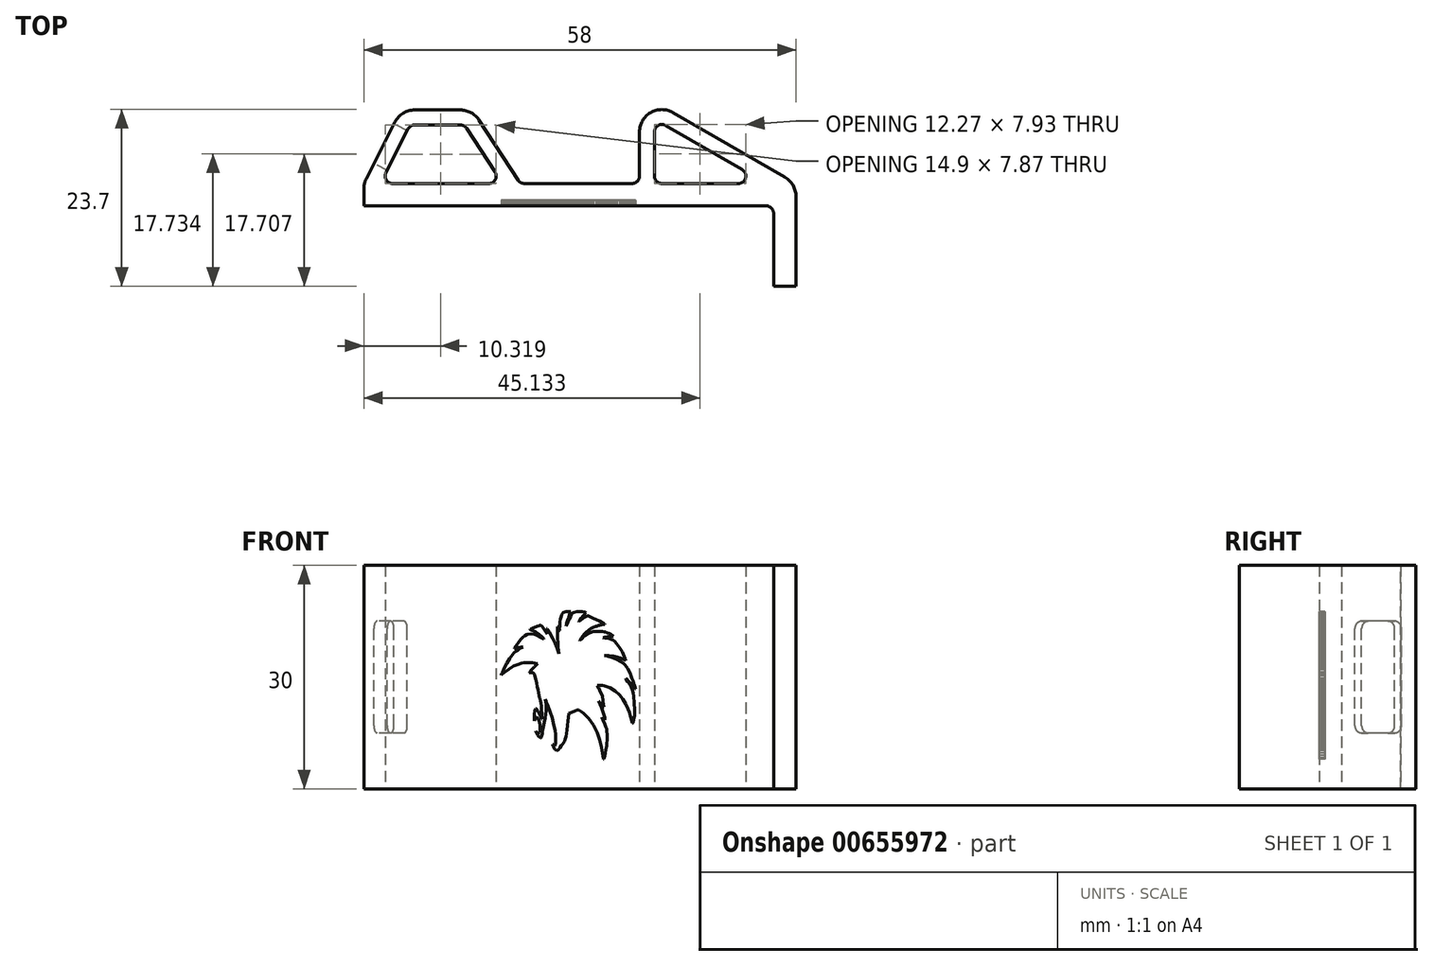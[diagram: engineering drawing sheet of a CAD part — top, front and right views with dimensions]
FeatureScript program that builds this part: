
annotation { "Feature Type Name" : "Feature", "Feature Type Description" : "" }
export const myFeature = defineFeature(function(context is Context, id is Id, definition is map)
    precondition{}
    {
        {
            assignVariable(context, id + "F0", {"name" : "SmallThickness", "anyValue" : 2 * mm});
        }
        {
            assignVariable(context, id + "F1", {"name" : "BatteryWidth", "anyValue" : 30});
        }
        {
            assignVariable(context, id + "F2", {"name" : "OuterFilet", "anyValue" : 3});
        }
        {
            assignVariable(context, id + "F3", {"name" : "InnerFilet", "anyValue" : 1 * mm});
        }
        {
            var Q0;
            Q0=qCreatedBy(makeId("Top.planeOp"),FACE);
            var sketch = newSketch(context, id + "F4", { "sketchPlane" : qUnion([Q0])});
            skLineSegment(sketch, "E0", {"start": v(-24, 9.87) * mm, "end": v(-29, 0) * mm});
            skLineSegment(sketch, "E1", {"start": v(-10.39, 0) * mm, "end": v(-15.5, 7.87) * mm});
            skLineSegment(sketch, "E2", {"start": v(-22.77, 7.87) * mm, "end": v(-26.76, 0) * mm});
            skLineSegment(sketch, "E3", {"start": v(-8, 0) * mm, "end": v(8, 0) * mm});
            skLineSegment(sketch, "E4", {"start": v(29, 0) * mm, "end": v(-29, 0) * mm, "construction": true});
            skLineSegment(sketch, "E5", {"start": v(10, 0) * mm, "end": v(25, 0) * mm});
            skLineSegment(sketch, "E6", {"start": v(29, 0) * mm, "end": v(8, 12.12) * mm});
            skLineSegment(sketch, "E7", {"start": v(8, 0) * mm, "end": v(8, 12.12) * mm});
            skLineSegment(sketch, "E8", {"start": v(10, 0) * mm, "end": v(10, 8.66) * mm});
            skLineSegment(sketch, "E9", {"start": v(10, 8.66) * mm, "end": v(25, 0) * mm});
            skLineSegment(sketch, "E10", {"start": v(42.35, 12.12) * mm, "end": v(-35.52, 12.12) * mm, "construction": true});
            skLineSegment(sketch, "E11", {"start": v(29, 0) * mm, "end": v(29, -13.77) * mm});
            skLineSegment(sketch, "E12", {"start": v(29, -13.77) * mm, "end": v(26, -13.77) * mm});
            skLineSegment(sketch, "E13", {"start": v(26, -13.77) * mm, "end": v(26, -3) * mm});
            skLineSegment(sketch, "E14", {"start": v(26, -3) * mm, "end": v(-29, -3) * mm});
            skLineSegment(sketch, "E15", {"start": v(-29, 0) * mm, "end": v(-29, -3) * mm});
            skLineSegment(sketch, "E16", {"start": v(-10.39, 0) * mm, "end": v(-26.76, 0) * mm});
            skLineSegment(sketch, "E17", {"start": v(25, 0) * mm, "end": v(10, 0) * mm});
            skLineSegment(sketch, "E18", {"start": v(-18.21, 9.87) * mm, "end": v(-18.21, 7.87) * mm, "construction": true});
            skLineSegment(sketch, "E19", {"start": v(-15.5, 7.87) * mm, "end": v(-22.77, 7.87) * mm});
            skLineSegment(sketch, "E20", {"start": v(-24, 9.87) * mm, "end": v(-14.42, 9.87) * mm});
            skLineSegment(sketch, "E21", {"start": v(-14.42, 9.87) * mm, "end": v(-8, 0) * mm});
            skSolve(sketch);
        }
        {
            var Q0;
            Q0 = qSketchRegion(id + "F4", true);
            extrude(context, id + "F5", {"entities" : qUnion([Q0]), "depth" : (getVariable(context, 'BatteryWidth')) * mm, "offsetDistance" : 25 * mm});
        }
        {
            var Q0;
            Q0=makeQuery(id+"F5.opExtrude","SWEPT_FACE",FACE,{"disambiguationData":[OSD([sQuery(id+"F4.wireOp",EDGE,"E14")])]});
            var sketch = newSketch(context, id + "F6", { "sketchPlane" : qUnion([Q0])});
            skLineSegment(sketch, "E22", {"start": v(-5.75, 22.15) * mm, "end": v(-5.57, 22.24) * mm});
            skLineSegment(sketch, "E23", {"start": v(-5.57, 22.24) * mm, "end": v(-5.41, 22.3) * mm});
            skLineSegment(sketch, "E24", {"start": v(-5.41, 22.3) * mm, "end": v(-5.32, 22.34) * mm});
            skLineSegment(sketch, "E25", {"start": v(-5.32, 22.34) * mm, "end": v(-5.3, 22.34) * mm});
            skLineSegment(sketch, "E26", {"start": v(-5.3, 22.34) * mm, "end": v(-5.3, 22.34) * mm});
            skLineSegment(sketch, "E27", {"start": v(-6.38, 21.9) * mm, "end": v(-6.07, 22) * mm});
            skLineSegment(sketch, "E28", {"start": v(-6.07, 22) * mm, "end": v(-5.75, 22.15) * mm});
            skLineSegment(sketch, "E29", {"start": v(-7.19, 21.57) * mm, "end": v(-7, 21.68) * mm});
            skLineSegment(sketch, "E30", {"start": v(-7, 21.68) * mm, "end": v(-6.74, 21.79) * mm});
            skLineSegment(sketch, "E31", {"start": v(-6.74, 21.79) * mm, "end": v(-6.55, 21.86) * mm});
            skLineSegment(sketch, "E32", {"start": v(-6.55, 21.86) * mm, "end": v(-6.38, 21.9) * mm});
            skLineSegment(sketch, "E33", {"start": v(-7.3, 21.42) * mm, "end": v(-7.26, 21.5) * mm});
            skLineSegment(sketch, "E34", {"start": v(-7.26, 21.5) * mm, "end": v(-7.19, 21.57) * mm});
            skLineSegment(sketch, "E35", {"start": v(-7.19, 21.37) * mm, "end": v(-7.28, 21.36) * mm});
            skLineSegment(sketch, "E36", {"start": v(-7.28, 21.36) * mm, "end": v(-7.3, 21.36) * mm});
            skLineSegment(sketch, "E37", {"start": v(-7.3, 21.36) * mm, "end": v(-7.32, 21.38) * mm});
            skLineSegment(sketch, "E38", {"start": v(-7.32, 21.38) * mm, "end": v(-7.3, 21.42) * mm});
            skLineSegment(sketch, "E39", {"start": v(-7.02, 21.3) * mm, "end": v(-7.07, 21.38) * mm});
            skLineSegment(sketch, "E40", {"start": v(-7.07, 21.38) * mm, "end": v(-7.19, 21.37) * mm});
            skLineSegment(sketch, "E41", {"start": v(-7.13, 21.14) * mm, "end": v(-7.06, 21.14) * mm});
            skLineSegment(sketch, "E42", {"start": v(-7.06, 21.14) * mm, "end": v(-7.03, 21.18) * mm});
            skLineSegment(sketch, "E43", {"start": v(-7.03, 21.18) * mm, "end": v(-7.02, 21.3) * mm});
            skLineSegment(sketch, "E44", {"start": v(-7.76, 20.68) * mm, "end": v(-7.5, 20.92) * mm});
            skLineSegment(sketch, "E45", {"start": v(-7.5, 20.92) * mm, "end": v(-7.32, 21.06) * mm});
            skLineSegment(sketch, "E46", {"start": v(-7.32, 21.06) * mm, "end": v(-7.21, 21.12) * mm});
            skLineSegment(sketch, "E47", {"start": v(-7.21, 21.12) * mm, "end": v(-7.13, 21.14) * mm});
            skLineSegment(sketch, "E48", {"start": v(-9.2, 18.81) * mm, "end": v(-8.9, 19.34) * mm});
            skLineSegment(sketch, "E49", {"start": v(-8.9, 19.34) * mm, "end": v(-8.5, 19.88) * mm});
            skLineSegment(sketch, "E50", {"start": v(-8.5, 19.88) * mm, "end": v(-7.76, 20.68) * mm});
            skLineSegment(sketch, "E51", {"start": v(-9.32, 18.57) * mm, "end": v(-9.2, 18.81) * mm});
            skLineSegment(sketch, "E52", {"start": v(-9.23, 18.5) * mm, "end": v(-9.32, 18.57) * mm});
            skLineSegment(sketch, "E53", {"start": v(-9.14, 18.43) * mm, "end": v(-9.23, 18.5) * mm});
            skLineSegment(sketch, "E54", {"start": v(-9.39, 18.09) * mm, "end": v(-9.14, 18.43) * mm});
            skLineSegment(sketch, "E55", {"start": v(-10.95, 14.96) * mm, "end": v(-10.65, 15.84) * mm});
            skLineSegment(sketch, "E56", {"start": v(-10.65, 15.84) * mm, "end": v(-10.23, 16.74) * mm});
            skLineSegment(sketch, "E57", {"start": v(-10.23, 16.74) * mm, "end": v(-9.83, 17.44) * mm});
            skLineSegment(sketch, "E58", {"start": v(-9.83, 17.44) * mm, "end": v(-9.39, 18.09) * mm});
            skLineSegment(sketch, "E59", {"start": v(3.79, 5.7) * mm, "end": v(3.7, 5.11) * mm});
            skLineSegment(sketch, "E60", {"start": v(3.7, 5.11) * mm, "end": v(3.56, 4.55) * mm});
            skLineSegment(sketch, "E61", {"start": v(3.56, 4.55) * mm, "end": v(3.42, 4.05) * mm});
            skLineSegment(sketch, "E62", {"start": v(3.42, 4.05) * mm, "end": v(3.32, 3.78) * mm});
            skLineSegment(sketch, "E63", {"start": v(3.32, 3.78) * mm, "end": v(3.23, 3.58) * mm});
            skLineSegment(sketch, "E64", {"start": v(3.23, 3.58) * mm, "end": v(3.15, 3.46) * mm});
            skLineSegment(sketch, "E65", {"start": v(3.15, 3.46) * mm, "end": v(3.1, 3.42) * mm});
            skLineSegment(sketch, "E66", {"start": v(3.8, 7.68) * mm, "end": v(3.83, 7.37) * mm});
            skLineSegment(sketch, "E67", {"start": v(3.83, 7.37) * mm, "end": v(3.84, 6.99) * mm});
            skLineSegment(sketch, "E68", {"start": v(3.84, 6.99) * mm, "end": v(3.84, 6.57) * mm});
            skLineSegment(sketch, "E69", {"start": v(3.84, 6.57) * mm, "end": v(3.82, 6.1) * mm});
            skLineSegment(sketch, "E70", {"start": v(3.82, 6.1) * mm, "end": v(3.79, 5.7) * mm});
            skArc(sketch, "E71", {"start": v(3.8, 7.68) * mm, "mid": v(3.76, 7.99) * mm, "end": v(3.7, 8.3) * mm});
            skArc(sketch, "E72", {"start": v(3.61, 9.04) * mm, "mid": v(3.64, 8.66) * mm, "end": v(3.7, 8.3) * mm});
            skArc(sketch, "E73", {"start": v(3.61, 9.04) * mm, "mid": v(3.59, 9.46) * mm, "end": v(3.5, 9.87) * mm});
            skLineSegment(sketch, "E74", {"start": v(3.44, 10.35) * mm, "end": v(3.43, 10.29) * mm});
            skLineSegment(sketch, "E75", {"start": v(3.43, 10.29) * mm, "end": v(3.44, 10.18) * mm});
            skLineSegment(sketch, "E76", {"start": v(3.44, 10.18) * mm, "end": v(3.46, 10.05) * mm});
            skLineSegment(sketch, "E77", {"start": v(3.46, 10.05) * mm, "end": v(3.5, 9.87) * mm});
            skLineSegment(sketch, "E78", {"start": v(3.07, 13.05) * mm, "end": v(3.22, 12.48) * mm});
            skLineSegment(sketch, "E79", {"start": v(3.22, 12.48) * mm, "end": v(3.35, 11.86) * mm});
            skLineSegment(sketch, "E80", {"start": v(3.35, 11.86) * mm, "end": v(3.43, 11.25) * mm});
            skLineSegment(sketch, "E81", {"start": v(3.43, 11.25) * mm, "end": v(3.47, 10.9) * mm});
            skLineSegment(sketch, "E82", {"start": v(3.47, 10.9) * mm, "end": v(3.48, 10.62) * mm});
            skLineSegment(sketch, "E83", {"start": v(3.48, 10.62) * mm, "end": v(3.47, 10.44) * mm});
            skLineSegment(sketch, "E84", {"start": v(3.47, 10.44) * mm, "end": v(3.44, 10.35) * mm});
            skArc(sketch, "E85", {"start": v(3.07, 13.05) * mm, "mid": v(3, 13.29) * mm, "end": v(2.92, 13.52) * mm});
            skLineSegment(sketch, "E86", {"start": v(3.09, 13.57) * mm, "end": v(2.96, 13.58) * mm});
            skLineSegment(sketch, "E87", {"start": v(2.96, 13.58) * mm, "end": v(2.92, 13.57) * mm});
            skLineSegment(sketch, "E88", {"start": v(2.92, 13.57) * mm, "end": v(2.91, 13.57) * mm});
            skLineSegment(sketch, "E89", {"start": v(2.91, 13.57) * mm, "end": v(2.91, 13.56) * mm});
            skLineSegment(sketch, "E90", {"start": v(2.91, 13.56) * mm, "end": v(2.92, 13.52) * mm});
            skLineSegment(sketch, "E91", {"start": v(5.54, 11.83) * mm, "end": v(4.9, 12.57) * mm});
            skLineSegment(sketch, "E92", {"start": v(4.9, 12.57) * mm, "end": v(4.2, 13.13) * mm});
            skLineSegment(sketch, "E93", {"start": v(4.2, 13.13) * mm, "end": v(3.63, 13.43) * mm});
            skLineSegment(sketch, "E94", {"start": v(3.63, 13.43) * mm, "end": v(3.09, 13.57) * mm});
            skLineSegment(sketch, "E95", {"start": v(7, 8.43) * mm, "end": v(6.68, 9.51) * mm});
            skLineSegment(sketch, "E96", {"start": v(6.68, 9.51) * mm, "end": v(6.29, 10.51) * mm});
            skLineSegment(sketch, "E97", {"start": v(6.29, 10.51) * mm, "end": v(5.93, 11.22) * mm});
            skLineSegment(sketch, "E98", {"start": v(5.93, 11.22) * mm, "end": v(5.54, 11.83) * mm});
            skLineSegment(sketch, "E99", {"start": v(7.14, 7.93) * mm, "end": v(7.14, 7.94) * mm});
            skLineSegment(sketch, "E100", {"start": v(7.14, 7.94) * mm, "end": v(7.14, 7.94) * mm});
            skLineSegment(sketch, "E101", {"start": v(7.14, 7.94) * mm, "end": v(7.12, 7.97) * mm});
            skLineSegment(sketch, "E102", {"start": v(7.12, 7.97) * mm, "end": v(7.1, 8.08) * mm});
            skLineSegment(sketch, "E103", {"start": v(7.1, 8.08) * mm, "end": v(7, 8.43) * mm});
            skLineSegment(sketch, "E104", {"start": v(7.44, 8.87) * mm, "end": v(7.28, 8.29) * mm});
            skLineSegment(sketch, "E105", {"start": v(7.28, 8.29) * mm, "end": v(7.2, 8.04) * mm});
            skLineSegment(sketch, "E106", {"start": v(7.2, 8.04) * mm, "end": v(7.16, 7.96) * mm});
            skLineSegment(sketch, "E107", {"start": v(7.16, 7.96) * mm, "end": v(7.15, 7.94) * mm});
            skLineSegment(sketch, "E108", {"start": v(7.15, 7.94) * mm, "end": v(7.14, 7.93) * mm});
            skLineSegment(sketch, "E109", {"start": v(7.57, 12.05) * mm, "end": v(7.6, 11.12) * mm});
            skLineSegment(sketch, "E110", {"start": v(7.6, 11.12) * mm, "end": v(7.59, 10.16) * mm});
            skLineSegment(sketch, "E111", {"start": v(7.59, 10.16) * mm, "end": v(7.53, 9.46) * mm});
            skLineSegment(sketch, "E112", {"start": v(7.53, 9.46) * mm, "end": v(7.44, 8.87) * mm});
            skLineSegment(sketch, "E113", {"start": v(7.52, 12.7) * mm, "end": v(7.57, 12.05) * mm});
            skLineSegment(sketch, "E114", {"start": v(7.63, 12.94) * mm, "end": v(7.53, 12.87) * mm});
            skLineSegment(sketch, "E115", {"start": v(7.53, 12.87) * mm, "end": v(7.52, 12.7) * mm});
            skArc(sketch, "E116", {"start": v(7.63, 12.94) * mm, "mid": v(7.71, 12.98) * mm, "end": v(7.79, 13.02) * mm});
            skLineSegment(sketch, "E117", {"start": v(7.4, 14.63) * mm, "end": v(7.57, 14.1) * mm});
            skLineSegment(sketch, "E118", {"start": v(7.57, 14.1) * mm, "end": v(7.7, 13.59) * mm});
            skLineSegment(sketch, "E119", {"start": v(7.7, 13.59) * mm, "end": v(7.75, 13.37) * mm});
            skLineSegment(sketch, "E120", {"start": v(7.75, 13.37) * mm, "end": v(7.78, 13.2) * mm});
            skLineSegment(sketch, "E121", {"start": v(7.78, 13.2) * mm, "end": v(7.8, 13.06) * mm});
            skLineSegment(sketch, "E122", {"start": v(7.8, 13.06) * mm, "end": v(7.8, 13.03) * mm});
            skLineSegment(sketch, "E123", {"start": v(7.8, 13.03) * mm, "end": v(7.79, 13.02) * mm});
            skArc(sketch, "E124", {"start": v(7.4, 14.63) * mm, "mid": v(7.08, 15.51) * mm, "end": v(6.68, 16.37) * mm});
            skLineSegment(sketch, "E125", {"start": v(6.5, 16.88) * mm, "end": v(6.48, 16.84) * mm});
            skLineSegment(sketch, "E126", {"start": v(6.48, 16.84) * mm, "end": v(6.48, 16.78) * mm});
            skLineSegment(sketch, "E127", {"start": v(6.48, 16.78) * mm, "end": v(6.5, 16.7) * mm});
            skLineSegment(sketch, "E128", {"start": v(6.5, 16.7) * mm, "end": v(6.57, 16.57) * mm});
            skLineSegment(sketch, "E129", {"start": v(6.57, 16.57) * mm, "end": v(6.68, 16.37) * mm});
            skLineSegment(sketch, "E130", {"start": v(6.5, 17.17) * mm, "end": v(6.55, 17) * mm});
            skLineSegment(sketch, "E131", {"start": v(6.55, 17) * mm, "end": v(6.55, 16.94) * mm});
            skLineSegment(sketch, "E132", {"start": v(6.55, 16.94) * mm, "end": v(6.5, 16.88) * mm});
            skLineSegment(sketch, "E133", {"start": v(4.95, 20.01) * mm, "end": v(5.5, 19.3) * mm});
            skLineSegment(sketch, "E134", {"start": v(5.5, 19.3) * mm, "end": v(5.98, 18.47) * mm});
            skLineSegment(sketch, "E135", {"start": v(5.98, 18.47) * mm, "end": v(6.3, 17.8) * mm});
            skLineSegment(sketch, "E136", {"start": v(6.3, 17.8) * mm, "end": v(6.5, 17.17) * mm});
            skLineSegment(sketch, "E137", {"start": v(4.77, 20.46) * mm, "end": v(4.73, 20.38) * mm});
            skLineSegment(sketch, "E138", {"start": v(4.73, 20.38) * mm, "end": v(4.74, 20.3) * mm});
            skLineSegment(sketch, "E139", {"start": v(4.74, 20.3) * mm, "end": v(4.8, 20.18) * mm});
            skLineSegment(sketch, "E140", {"start": v(4.8, 20.18) * mm, "end": v(4.95, 20.01) * mm});
            skLineSegment(sketch, "E141", {"start": v(4.74, 20.76) * mm, "end": v(4.82, 20.6) * mm});
            skLineSegment(sketch, "E142", {"start": v(4.82, 20.6) * mm, "end": v(4.77, 20.46) * mm});
            skLineSegment(sketch, "E143", {"start": v(-2.9, 22.72) * mm, "end": v(-2.88, 22.85) * mm});
            skLineSegment(sketch, "E144", {"start": v(-2.88, 22.85) * mm, "end": v(-2.83, 23.05) * mm});
            skLineSegment(sketch, "E145", {"start": v(-2.83, 23.05) * mm, "end": v(-2.73, 23.46) * mm});
            skLineSegment(sketch, "E146", {"start": v(-3.06, 22.54) * mm, "end": v(-3, 22.49) * mm});
            skLineSegment(sketch, "E147", {"start": v(-3, 22.49) * mm, "end": v(-2.97, 22.49) * mm});
            skLineSegment(sketch, "E148", {"start": v(-2.97, 22.49) * mm, "end": v(-2.95, 22.52) * mm});
            skLineSegment(sketch, "E149", {"start": v(-2.95, 22.52) * mm, "end": v(-2.93, 22.57) * mm});
            skLineSegment(sketch, "E150", {"start": v(-2.93, 22.57) * mm, "end": v(-2.9, 22.72) * mm});
            skLineSegment(sketch, "E151", {"start": v(-3.15, 22.58) * mm, "end": v(-3.14, 22.6) * mm});
            skLineSegment(sketch, "E152", {"start": v(-3.14, 22.6) * mm, "end": v(-3.12, 22.6) * mm});
            skLineSegment(sketch, "E153", {"start": v(-3.12, 22.6) * mm, "end": v(-3.1, 22.6) * mm});
            skLineSegment(sketch, "E154", {"start": v(-3.1, 22.6) * mm, "end": v(-3.06, 22.54) * mm});
            skLineSegment(sketch, "E155", {"start": v(-3.27, 21.07) * mm, "end": v(-3.24, 21.65) * mm});
            skLineSegment(sketch, "E156", {"start": v(-3.24, 21.65) * mm, "end": v(-3.2, 22.14) * mm});
            skLineSegment(sketch, "E157", {"start": v(-3.2, 22.14) * mm, "end": v(-3.18, 22.45) * mm});
            skLineSegment(sketch, "E158", {"start": v(-3.18, 22.45) * mm, "end": v(-3.15, 22.58) * mm});
            skLineSegment(sketch, "E159", {"start": v(-3.34, 20.3) * mm, "end": v(-3.33, 20.3) * mm});
            skLineSegment(sketch, "E160", {"start": v(-3.33, 20.3) * mm, "end": v(-3.32, 20.34) * mm});
            skLineSegment(sketch, "E161", {"start": v(-3.32, 20.34) * mm, "end": v(-3.3, 20.43) * mm});
            skLineSegment(sketch, "E162", {"start": v(-3.3, 20.43) * mm, "end": v(-3.29, 20.6) * mm});
            skLineSegment(sketch, "E163", {"start": v(-3.29, 20.6) * mm, "end": v(-3.28, 20.8) * mm});
            skLineSegment(sketch, "E164", {"start": v(-3.28, 20.8) * mm, "end": v(-3.27, 21.07) * mm});
            skLineSegment(sketch, "E165", {"start": v(-3.73, 20.9) * mm, "end": v(-3.57, 20.6) * mm});
            skLineSegment(sketch, "E166", {"start": v(-3.57, 20.6) * mm, "end": v(-3.45, 20.4) * mm});
            skLineSegment(sketch, "E167", {"start": v(-3.45, 20.4) * mm, "end": v(-3.38, 20.32) * mm});
            skLineSegment(sketch, "E168", {"start": v(-3.38, 20.32) * mm, "end": v(-3.34, 20.3) * mm});
            skLineSegment(sketch, "E169", {"start": v(-5.3, 22.34) * mm, "end": v(-5.28, 22.33) * mm});
            skLineSegment(sketch, "E170", {"start": v(-5.28, 22.33) * mm, "end": v(-5.27, 22.32) * mm});
            skLineSegment(sketch, "E171", {"start": v(-5.27, 22.32) * mm, "end": v(-5.25, 22.3) * mm});
            skLineSegment(sketch, "E172", {"start": v(-5.25, 22.3) * mm, "end": v(-5.19, 22.23) * mm});
            skLineSegment(sketch, "E173", {"start": v(-5.19, 22.23) * mm, "end": v(-5.04, 22.05) * mm});
            skLineSegment(sketch, "E174", {"start": v(-5.04, 22.05) * mm, "end": v(-4.85, 21.85) * mm});
            skLineSegment(sketch, "E175", {"start": v(-4.85, 21.85) * mm, "end": v(-4.72, 21.79) * mm});
            skLineSegment(sketch, "E176", {"start": v(-4.72, 21.79) * mm, "end": v(-4.65, 21.83) * mm});
            skLineSegment(sketch, "E177", {"start": v(-4.65, 21.83) * mm, "end": v(-4.6, 22) * mm});
            skLineSegment(sketch, "E178", {"start": v(-4.6, 22) * mm, "end": v(-4.57, 22.08) * mm});
            skLineSegment(sketch, "E179", {"start": v(-4.57, 22.08) * mm, "end": v(-4.55, 22.1) * mm});
            skLineSegment(sketch, "E180", {"start": v(-4.55, 22.1) * mm, "end": v(-4.53, 22.11) * mm});
            skLineSegment(sketch, "E181", {"start": v(-4.53, 22.11) * mm, "end": v(-4.49, 22.1) * mm});
            skLineSegment(sketch, "E182", {"start": v(-4.49, 22.1) * mm, "end": v(-4.45, 22.06) * mm});
            skLineSegment(sketch, "E183", {"start": v(-4.45, 22.06) * mm, "end": v(-4.36, 21.95) * mm});
            skLineSegment(sketch, "E184", {"start": v(-4.36, 21.95) * mm, "end": v(-4.15, 21.65) * mm});
            skLineSegment(sketch, "E185", {"start": v(-4.15, 21.65) * mm, "end": v(-3.94, 21.3) * mm});
            skLineSegment(sketch, "E186", {"start": v(-3.94, 21.3) * mm, "end": v(-3.73, 20.9) * mm});
            skLineSegment(sketch, "E187", {"start": v(-2.73, 23.46) * mm, "end": v(-2.66, 23.72) * mm});
            skLineSegment(sketch, "E188", {"start": v(-2.66, 23.72) * mm, "end": v(-2.6, 23.9) * mm});
            skLineSegment(sketch, "E189", {"start": v(-2.6, 23.9) * mm, "end": v(-2.5, 24.06) * mm});
            skLineSegment(sketch, "E190", {"start": v(-2.5, 24.06) * mm, "end": v(-2.35, 24.12) * mm});
            skLineSegment(sketch, "E191", {"start": v(-2.35, 24.12) * mm, "end": v(-2.1, 24.17) * mm});
            skLineSegment(sketch, "E192", {"start": v(-2.1, 24.17) * mm, "end": v(-1.67, 24.23) * mm});
            skLineSegment(sketch, "E193", {"start": v(-1.67, 24.23) * mm, "end": v(-1.35, 24.25) * mm});
            skLineSegment(sketch, "E194", {"start": v(-1.35, 24.25) * mm, "end": v(-1.16, 24.25) * mm});
            skLineSegment(sketch, "E195", {"start": v(-1.16, 24.25) * mm, "end": v(-1.08, 24.22) * mm});
            skLineSegment(sketch, "E196", {"start": v(-1.08, 24.22) * mm, "end": v(-0.97, 24.18) * mm});
            skLineSegment(sketch, "E197", {"start": v(-0.97, 24.18) * mm, "end": v(-0.8, 24.18) * mm});
            skLineSegment(sketch, "E198", {"start": v(-0.8, 24.18) * mm, "end": v(-0.6, 24.2) * mm});
            skLineSegment(sketch, "E199", {"start": v(-0.6, 24.2) * mm, "end": v(-0.37, 24.23) * mm});
            skLineSegment(sketch, "E200", {"start": v(-0.37, 24.23) * mm, "end": v(0, 24.27) * mm});
            skLineSegment(sketch, "E201", {"start": v(0, 24.27) * mm, "end": v(0.4, 24.29) * mm});
            skLineSegment(sketch, "E202", {"start": v(0.4, 24.29) * mm, "end": v(0.67, 24.27) * mm});
            skLineSegment(sketch, "E203", {"start": v(0.67, 24.27) * mm, "end": v(0.86, 24.24) * mm});
            skLineSegment(sketch, "E204", {"start": v(0.86, 24.24) * mm, "end": v(1, 24.16) * mm});
            skLineSegment(sketch, "E205", {"start": v(1, 24.16) * mm, "end": v(1.04, 24.05) * mm});
            skLineSegment(sketch, "E206", {"start": v(1.04, 24.05) * mm, "end": v(1.12, 23.89) * mm});
            skLineSegment(sketch, "E207", {"start": v(1.12, 23.89) * mm, "end": v(1.25, 23.74) * mm});
            skLineSegment(sketch, "E208", {"start": v(1.25, 23.74) * mm, "end": v(1.56, 23.53) * mm});
            skLineSegment(sketch, "E209", {"start": v(1.56, 23.53) * mm, "end": v(2.2, 23.23) * mm});
            skLineSegment(sketch, "E210", {"start": v(2.2, 23.23) * mm, "end": v(2.72, 22.96) * mm});
            skLineSegment(sketch, "E211", {"start": v(2.72, 22.96) * mm, "end": v(3.16, 22.7) * mm});
            skLineSegment(sketch, "E212", {"start": v(3.16, 22.7) * mm, "end": v(3.58, 22.43) * mm});
            skLineSegment(sketch, "E213", {"start": v(3.58, 22.43) * mm, "end": v(3.92, 22.16) * mm});
            skLineSegment(sketch, "E214", {"start": v(3.92, 22.16) * mm, "end": v(4.11, 21.99) * mm});
            skLineSegment(sketch, "E215", {"start": v(4.11, 21.99) * mm, "end": v(4.02, 21.91) * mm});
            skLineSegment(sketch, "E216", {"start": v(4.02, 21.91) * mm, "end": v(3.88, 21.83) * mm});
            skLineSegment(sketch, "E217", {"start": v(3.88, 21.83) * mm, "end": v(3.7, 21.76) * mm});
            skLineSegment(sketch, "E218", {"start": v(3.7, 21.76) * mm, "end": v(3.27, 21.64) * mm});
            skLineSegment(sketch, "E219", {"start": v(3.27, 21.64) * mm, "end": v(3.17, 21.6) * mm});
            skLineSegment(sketch, "E220", {"start": v(3.17, 21.6) * mm, "end": v(3.16, 21.6) * mm});
            skLineSegment(sketch, "E221", {"start": v(3.16, 21.6) * mm, "end": v(3.15, 21.58) * mm});
            skLineSegment(sketch, "E222", {"start": v(3.15, 21.58) * mm, "end": v(3.17, 21.56) * mm});
            skLineSegment(sketch, "E223", {"start": v(3.17, 21.56) * mm, "end": v(3.21, 21.54) * mm});
            skLineSegment(sketch, "E224", {"start": v(3.21, 21.54) * mm, "end": v(3.4, 21.48) * mm});
            skLineSegment(sketch, "E225", {"start": v(3.4, 21.48) * mm, "end": v(3.8, 21.32) * mm});
            skLineSegment(sketch, "E226", {"start": v(3.8, 21.32) * mm, "end": v(4.22, 21.1) * mm});
            skLineSegment(sketch, "E227", {"start": v(4.22, 21.1) * mm, "end": v(4.52, 20.93) * mm});
            skLineSegment(sketch, "E228", {"start": v(4.52, 20.93) * mm, "end": v(4.74, 20.76) * mm});
            skLineSegment(sketch, "E229", {"start": v(3.1, 3.42) * mm, "end": v(3.09, 3.42) * mm});
            skLineSegment(sketch, "E230", {"start": v(3.09, 3.42) * mm, "end": v(3.08, 3.43) * mm});
            skLineSegment(sketch, "E231", {"start": v(3.08, 3.43) * mm, "end": v(3.05, 3.5) * mm});
            skLineSegment(sketch, "E232", {"start": v(3.05, 3.5) * mm, "end": v(3.03, 3.62) * mm});
            skLineSegment(sketch, "E233", {"start": v(3.03, 3.62) * mm, "end": v(2.78, 5.08) * mm});
            skLineSegment(sketch, "E234", {"start": v(2.78, 5.08) * mm, "end": v(2.42, 6.46) * mm});
            skLineSegment(sketch, "E235", {"start": v(2.42, 6.46) * mm, "end": v(2.08, 7.4) * mm});
            skLineSegment(sketch, "E236", {"start": v(2.08, 7.4) * mm, "end": v(1.7, 8.18) * mm});
            skLineSegment(sketch, "E237", {"start": v(1.7, 8.18) * mm, "end": v(1.37, 8.67) * mm});
            skLineSegment(sketch, "E238", {"start": v(1.37, 8.67) * mm, "end": v(0.99, 9.16) * mm});
            skLineSegment(sketch, "E239", {"start": v(0.99, 9.16) * mm, "end": v(0.6, 9.6) * mm});
            skLineSegment(sketch, "E240", {"start": v(0.6, 9.6) * mm, "end": v(0.35, 9.84) * mm});
            skLineSegment(sketch, "E241", {"start": v(0.35, 9.84) * mm, "end": v(0.14, 10.02) * mm});
            skLineSegment(sketch, "E242", {"start": v(0.14, 10.02) * mm, "end": v(0, 10.11) * mm});
            skLineSegment(sketch, "E243", {"start": v(0, 10.11) * mm, "end": v(-0.12, 10.16) * mm});
            skLineSegment(sketch, "E244", {"start": v(-0.12, 10.16) * mm, "end": v(-0.4, 10.15) * mm});
            skLineSegment(sketch, "E245", {"start": v(-0.4, 10.15) * mm, "end": v(-0.7, 10.05) * mm});
            skLineSegment(sketch, "E246", {"start": v(-0.7, 10.05) * mm, "end": v(-0.93, 9.91) * mm});
            skLineSegment(sketch, "E247", {"start": v(-0.93, 9.91) * mm, "end": v(-1.12, 9.75) * mm});
            skLineSegment(sketch, "E248", {"start": v(-1.12, 9.75) * mm, "end": v(-1.24, 9.56) * mm});
            skLineSegment(sketch, "E249", {"start": v(-1.24, 9.56) * mm, "end": v(-1.29, 9.34) * mm});
            skLineSegment(sketch, "E250", {"start": v(-1.29, 9.34) * mm, "end": v(-1.57, 7.23) * mm});
            skLineSegment(sketch, "E251", {"start": v(-1.57, 7.23) * mm, "end": v(-1.62, 6.8) * mm});
            skLineSegment(sketch, "E252", {"start": v(-1.62, 6.8) * mm, "end": v(-1.67, 6.5) * mm});
            skLineSegment(sketch, "E253", {"start": v(-1.67, 6.5) * mm, "end": v(-1.73, 6.28) * mm});
            skLineSegment(sketch, "E254", {"start": v(-1.73, 6.28) * mm, "end": v(-1.84, 6.08) * mm});
            skLineSegment(sketch, "E255", {"start": v(-1.84, 6.08) * mm, "end": v(-2, 5.87) * mm});
            skLineSegment(sketch, "E256", {"start": v(-2, 5.87) * mm, "end": v(-2.57, 5.17) * mm});
            skLineSegment(sketch, "E257", {"start": v(-2.57, 5.17) * mm, "end": v(-2.73, 4.96) * mm});
            skLineSegment(sketch, "E258", {"start": v(-2.73, 4.96) * mm, "end": v(-2.86, 4.82) * mm});
            skLineSegment(sketch, "E259", {"start": v(-2.86, 4.82) * mm, "end": v(-3, 4.7) * mm});
            skLineSegment(sketch, "E260", {"start": v(-3, 4.7) * mm, "end": v(-3.15, 4.69) * mm});
            skLineSegment(sketch, "E261", {"start": v(-3.15, 4.69) * mm, "end": v(-3.32, 4.8) * mm});
            skLineSegment(sketch, "E262", {"start": v(-3.32, 4.8) * mm, "end": v(-3.49, 4.97) * mm});
            skLineSegment(sketch, "E263", {"start": v(-3.49, 4.97) * mm, "end": v(-3.64, 5.24) * mm});
            skLineSegment(sketch, "E264", {"start": v(-3.64, 5.24) * mm, "end": v(-3.75, 5.52) * mm});
            skLineSegment(sketch, "E265", {"start": v(-3.75, 5.52) * mm, "end": v(-3.85, 5.85) * mm});
            skLineSegment(sketch, "E266", {"start": v(-3.85, 5.85) * mm, "end": v(-3.92, 6.11) * mm});
            skLineSegment(sketch, "E267", {"start": v(-3.92, 6.11) * mm, "end": v(-3.96, 6.3) * mm});
            skLineSegment(sketch, "E268", {"start": v(-3.96, 6.3) * mm, "end": v(-3.96, 6.41) * mm});
            skLineSegment(sketch, "E269", {"start": v(-3.96, 6.41) * mm, "end": v(-3.95, 6.46) * mm});
            skLineSegment(sketch, "E270", {"start": v(-3.95, 6.46) * mm, "end": v(-3.92, 6.48) * mm});
            skLineSegment(sketch, "E271", {"start": v(-3.92, 6.48) * mm, "end": v(-3.88, 6.48) * mm});
            skLineSegment(sketch, "E272", {"start": v(-3.88, 6.48) * mm, "end": v(-3.7, 6.4) * mm});
            skLineSegment(sketch, "E273", {"start": v(-3.7, 6.4) * mm, "end": v(-3.54, 6.3) * mm});
            skLineSegment(sketch, "E274", {"start": v(-3.54, 6.3) * mm, "end": v(-3.52, 6.44) * mm});
            skLineSegment(sketch, "E275", {"start": v(-3.52, 6.44) * mm, "end": v(-3.48, 6.73) * mm});
            skLineSegment(sketch, "E276", {"start": v(-3.48, 6.73) * mm, "end": v(-3.47, 6.97) * mm});
            skLineSegment(sketch, "E277", {"start": v(-3.47, 6.97) * mm, "end": v(-3.48, 7.17) * mm});
            skLineSegment(sketch, "E278", {"start": v(-3.48, 7.17) * mm, "end": v(-3.5, 7.4) * mm});
            skArc(sketch, "E279", {"start": v(-3.5, 7.4) * mm, "mid": v(-3.6, 8.14) * mm, "end": v(-3.77, 8.86) * mm});
            skLineSegment(sketch, "E280", {"start": v(-3.77, 8.86) * mm, "end": v(-4.05, 9.7) * mm});
            skLineSegment(sketch, "E281", {"start": v(-4.05, 9.7) * mm, "end": v(-4.19, 10.06) * mm});
            skLineSegment(sketch, "E282", {"start": v(-4.19, 10.06) * mm, "end": v(-4.23, 10.17) * mm});
            skLineSegment(sketch, "E283", {"start": v(-4.23, 10.17) * mm, "end": v(-4.25, 10.2) * mm});
            skLineSegment(sketch, "E284", {"start": v(-4.25, 10.2) * mm, "end": v(-4.26, 10.21) * mm});
            skLineSegment(sketch, "E285", {"start": v(-4.26, 10.21) * mm, "end": v(-4.27, 10.2) * mm});
            skLineSegment(sketch, "E286", {"start": v(-4.27, 10.2) * mm, "end": v(-4.29, 10.2) * mm});
            skLineSegment(sketch, "E287", {"start": v(-4.29, 10.2) * mm, "end": v(-4.34, 10.02) * mm});
            skLineSegment(sketch, "E288", {"start": v(-4.34, 10.02) * mm, "end": v(-4.44, 9.52) * mm});
            skLineSegment(sketch, "E289", {"start": v(-4.44, 9.52) * mm, "end": v(-4.73, 7.15) * mm});
            skLineSegment(sketch, "E290", {"start": v(-4.73, 7.15) * mm, "end": v(-4.78, 6.3) * mm});
            skLineSegment(sketch, "E291", {"start": v(-4.78, 6.3) * mm, "end": v(-4.83, 6.1) * mm});
            skLineSegment(sketch, "E292", {"start": v(-4.83, 6.1) * mm, "end": v(-4.9, 5.9) * mm});
            skLineSegment(sketch, "E293", {"start": v(-4.9, 5.9) * mm, "end": v(-4.96, 5.75) * mm});
            skLineSegment(sketch, "E294", {"start": v(-4.96, 5.75) * mm, "end": v(-5.01, 5.65) * mm});
            skLineSegment(sketch, "E295", {"start": v(-5.01, 5.65) * mm, "end": v(-5.08, 5.56) * mm});
            skLineSegment(sketch, "E296", {"start": v(-5.08, 5.56) * mm, "end": v(-5.2, 5.67) * mm});
            skArc(sketch, "E297", {"start": v(-5.48, 6.03) * mm, "mid": v(-5.35, 5.85) * mm, "end": v(-5.2, 5.67) * mm});
            skLineSegment(sketch, "E298", {"start": v(-5.48, 6.03) * mm, "end": v(-5.7, 6.37) * mm});
            skLineSegment(sketch, "E299", {"start": v(-5.7, 6.37) * mm, "end": v(-5.84, 6.67) * mm});
            skLineSegment(sketch, "E300", {"start": v(-5.84, 6.67) * mm, "end": v(-5.95, 7.14) * mm});
            skLineSegment(sketch, "E301", {"start": v(-5.95, 7.14) * mm, "end": v(-6.04, 7.46) * mm});
            skLineSegment(sketch, "E302", {"start": v(-6.04, 7.46) * mm, "end": v(-6.17, 7.78) * mm});
            skLineSegment(sketch, "E303", {"start": v(-6.17, 7.78) * mm, "end": v(-6.3, 8.08) * mm});
            skLineSegment(sketch, "E304", {"start": v(-6.3, 8.08) * mm, "end": v(-6.33, 8.18) * mm});
            skLineSegment(sketch, "E305", {"start": v(-6.33, 8.18) * mm, "end": v(-6.34, 8.2) * mm});
            skLineSegment(sketch, "E306", {"start": v(-6.34, 8.2) * mm, "end": v(-6.34, 8.21) * mm});
            skLineSegment(sketch, "E307", {"start": v(-6.34, 8.21) * mm, "end": v(-6.33, 8.21) * mm});
            skLineSegment(sketch, "E308", {"start": v(-6.33, 8.21) * mm, "end": v(-6.3, 8.2) * mm});
            skLineSegment(sketch, "E309", {"start": v(-6.3, 8.2) * mm, "end": v(-6.23, 8.18) * mm});
            skLineSegment(sketch, "E310", {"start": v(-6.23, 8.18) * mm, "end": v(-6, 8.08) * mm});
            skLineSegment(sketch, "E311", {"start": v(-6, 8.08) * mm, "end": v(-5.73, 7.96) * mm});
            skLineSegment(sketch, "E312", {"start": v(-5.73, 7.96) * mm, "end": v(-5.66, 7.95) * mm});
            skLineSegment(sketch, "E313", {"start": v(-5.66, 7.95) * mm, "end": v(-5.63, 7.96) * mm});
            skLineSegment(sketch, "E314", {"start": v(-5.63, 7.96) * mm, "end": v(-5.62, 7.97) * mm});
            skLineSegment(sketch, "E315", {"start": v(-5.62, 7.97) * mm, "end": v(-5.62, 8) * mm});
            skLineSegment(sketch, "E316", {"start": v(-5.62, 8) * mm, "end": v(-5.61, 8.04) * mm});
            skLineSegment(sketch, "E317", {"start": v(-5.61, 8.04) * mm, "end": v(-5.62, 8.18) * mm});
            skLineSegment(sketch, "E318", {"start": v(-5.62, 8.18) * mm, "end": v(-5.65, 8.5) * mm});
            skLineSegment(sketch, "E319", {"start": v(-5.65, 8.5) * mm, "end": v(-5.71, 8.84) * mm});
            skLineSegment(sketch, "E320", {"start": v(-5.71, 8.84) * mm, "end": v(-5.74, 8.96) * mm});
            skLineSegment(sketch, "E321", {"start": v(-5.74, 8.96) * mm, "end": v(-5.75, 9) * mm});
            skLineSegment(sketch, "E322", {"start": v(-5.75, 9) * mm, "end": v(-5.76, 9) * mm});
            skLineSegment(sketch, "E323", {"start": v(-5.76, 9) * mm, "end": v(-5.76, 9) * mm});
            skLineSegment(sketch, "E324", {"start": v(-5.76, 9) * mm, "end": v(-5.78, 9) * mm});
            skLineSegment(sketch, "E325", {"start": v(-5.78, 9) * mm, "end": v(-5.8, 8.99) * mm});
            skLineSegment(sketch, "E326", {"start": v(-5.8, 8.99) * mm, "end": v(-5.85, 8.93) * mm});
            skLineSegment(sketch, "E327", {"start": v(-5.85, 8.93) * mm, "end": v(-5.98, 8.73) * mm});
            skLineSegment(sketch, "E328", {"start": v(-5.98, 8.73) * mm, "end": v(-6.1, 8.55) * mm});
            skLineSegment(sketch, "E329", {"start": v(-6.1, 8.55) * mm, "end": v(-6.16, 8.49) * mm});
            skLineSegment(sketch, "E330", {"start": v(-6.16, 8.49) * mm, "end": v(-6.18, 8.48) * mm});
            skLineSegment(sketch, "E331", {"start": v(-6.18, 8.48) * mm, "end": v(-6.18, 8.48) * mm});
            skLineSegment(sketch, "E332", {"start": v(-6.18, 8.48) * mm, "end": v(-6.18, 8.49) * mm});
            skLineSegment(sketch, "E333", {"start": v(-6.18, 8.49) * mm, "end": v(-6.23, 8.7) * mm});
            skLineSegment(sketch, "E334", {"start": v(-6.23, 8.7) * mm, "end": v(-6.27, 9.04) * mm});
            skLineSegment(sketch, "E335", {"start": v(-6.27, 9.04) * mm, "end": v(-6.28, 9.37) * mm});
            skLineSegment(sketch, "E336", {"start": v(-6.28, 9.37) * mm, "end": v(-6.28, 9.74) * mm});
            skLineSegment(sketch, "E337", {"start": v(-6.28, 9.74) * mm, "end": v(-6.26, 10.15) * mm});
            skLineSegment(sketch, "E338", {"start": v(-6.26, 10.15) * mm, "end": v(-6.24, 10.44) * mm});
            skLineSegment(sketch, "E339", {"start": v(-6.24, 10.44) * mm, "end": v(-6.2, 10.66) * mm});
            skLineSegment(sketch, "E340", {"start": v(-6.2, 10.66) * mm, "end": v(-6.14, 10.92) * mm});
            skLineSegment(sketch, "E341", {"start": v(-6.14, 10.92) * mm, "end": v(-6.09, 11.14) * mm});
            skLineSegment(sketch, "E342", {"start": v(-6.09, 11.14) * mm, "end": v(-6.04, 11.32) * mm});
            skLineSegment(sketch, "E343", {"start": v(-6.04, 11.32) * mm, "end": v(-6, 11.42) * mm});
            skLineSegment(sketch, "E344", {"start": v(-6, 11.42) * mm, "end": v(-6, 11.44) * mm});
            skLineSegment(sketch, "E345", {"start": v(-6, 11.44) * mm, "end": v(-6, 11.45) * mm});
            skLineSegment(sketch, "E346", {"start": v(-6, 11.45) * mm, "end": v(-5.99, 11.46) * mm});
            skLineSegment(sketch, "E347", {"start": v(-5.99, 11.46) * mm, "end": v(-5.98, 11.45) * mm});
            skLineSegment(sketch, "E348", {"start": v(-5.98, 11.45) * mm, "end": v(-5.97, 11.44) * mm});
            skLineSegment(sketch, "E349", {"start": v(-5.97, 11.44) * mm, "end": v(-5.88, 11.36) * mm});
            skLineSegment(sketch, "E350", {"start": v(-5.88, 11.36) * mm, "end": v(-5.76, 11.2) * mm});
            skLineSegment(sketch, "E351", {"start": v(-5.76, 11.2) * mm, "end": v(-5.6, 11) * mm});
            skLineSegment(sketch, "E352", {"start": v(-5.6, 11) * mm, "end": v(-5.52, 10.94) * mm});
            skLineSegment(sketch, "E353", {"start": v(-5.52, 10.94) * mm, "end": v(-5.5, 10.94) * mm});
            skLineSegment(sketch, "E354", {"start": v(-5.5, 10.94) * mm, "end": v(-5.5, 10.95) * mm});
            skLineSegment(sketch, "E355", {"start": v(-5.5, 10.95) * mm, "end": v(-5.5, 10.99) * mm});
            skLineSegment(sketch, "E356", {"start": v(-5.5, 10.99) * mm, "end": v(-5.5, 11.03) * mm});
            skArc(sketch, "E357", {"start": v(-5.56, 11.42) * mm, "mid": v(-5.53, 11.23) * mm, "end": v(-5.5, 11.03) * mm});
            skLineSegment(sketch, "E358", {"start": v(-5.56, 11.42) * mm, "end": v(-5.62, 11.8) * mm});
            skLineSegment(sketch, "E359", {"start": v(-5.62, 11.8) * mm, "end": v(-5.7, 12.33) * mm});
            skLineSegment(sketch, "E360", {"start": v(-5.7, 12.33) * mm, "end": v(-5.82, 12.93) * mm});
            skLineSegment(sketch, "E361", {"start": v(-5.82, 12.93) * mm, "end": v(-5.93, 13.54) * mm});
            skLineSegment(sketch, "E362", {"start": v(-5.93, 13.54) * mm, "end": v(-6.03, 14.04) * mm});
            skLineSegment(sketch, "E363", {"start": v(-6.03, 14.04) * mm, "end": v(-6.11, 14.45) * mm});
            skLineSegment(sketch, "E364", {"start": v(-6.11, 14.45) * mm, "end": v(-6.16, 14.68) * mm});
            skLineSegment(sketch, "E365", {"start": v(-6.16, 14.68) * mm, "end": v(-6.2, 14.81) * mm});
            skArc(sketch, "E366", {"start": v(-6.2, 14.81) * mm, "mid": v(-6.27, 14.97) * mm, "end": v(-6.38, 15.1) * mm});
            skLineSegment(sketch, "E367", {"start": v(-6.38, 15.1) * mm, "end": v(-6.47, 15.17) * mm});
            skLineSegment(sketch, "E368", {"start": v(-6.47, 15.17) * mm, "end": v(-6.55, 15.2) * mm});
            skLineSegment(sketch, "E369", {"start": v(-6.55, 15.2) * mm, "end": v(-6.62, 15.2) * mm});
            skLineSegment(sketch, "E370", {"start": v(-6.62, 15.2) * mm, "end": v(-6.74, 15.2) * mm});
            skLineSegment(sketch, "E371", {"start": v(-6.74, 15.2) * mm, "end": v(-6.97, 15.18) * mm});
            skLineSegment(sketch, "E372", {"start": v(-6.97, 15.18) * mm, "end": v(-7, 15.28) * mm});
            skLineSegment(sketch, "E373", {"start": v(-7, 15.28) * mm, "end": v(-7, 15.54) * mm});
            skLineSegment(sketch, "E374", {"start": v(-7, 15.54) * mm, "end": v(-6.9, 15.87) * mm});
            skLineSegment(sketch, "E375", {"start": v(-6.9, 15.87) * mm, "end": v(-6.65, 16.4) * mm});
            skLineSegment(sketch, "E376", {"start": v(-6.65, 16.4) * mm, "end": v(-6.57, 16.52) * mm});
            skLineSegment(sketch, "E377", {"start": v(-6.57, 16.52) * mm, "end": v(-6.54, 16.58) * mm});
            skLineSegment(sketch, "E378", {"start": v(-6.54, 16.58) * mm, "end": v(-6.54, 16.61) * mm});
            skLineSegment(sketch, "E379", {"start": v(-6.54, 16.61) * mm, "end": v(-6.56, 16.63) * mm});
            skLineSegment(sketch, "E380", {"start": v(-6.56, 16.63) * mm, "end": v(-6.66, 16.64) * mm});
            skLineSegment(sketch, "E381", {"start": v(-6.66, 16.64) * mm, "end": v(-6.8, 16.65) * mm});
            skLineSegment(sketch, "E382", {"start": v(-6.8, 16.65) * mm, "end": v(-7.1, 16.65) * mm});
            skLineSegment(sketch, "E383", {"start": v(-7.1, 16.65) * mm, "end": v(-7.36, 16.63) * mm});
            skLineSegment(sketch, "E384", {"start": v(-7.36, 16.63) * mm, "end": v(-7.56, 16.61) * mm});
            skLineSegment(sketch, "E385", {"start": v(-7.56, 16.61) * mm, "end": v(-8.42, 16.34) * mm});
            skLineSegment(sketch, "E386", {"start": v(-8.42, 16.34) * mm, "end": v(-9.31, 15.86) * mm});
            skLineSegment(sketch, "E387", {"start": v(-9.31, 15.86) * mm, "end": v(-10.03, 15.35) * mm});
            skLineSegment(sketch, "E388", {"start": v(-10.03, 15.35) * mm, "end": v(-10.74, 14.73) * mm});
            skLineSegment(sketch, "E389", {"start": v(-10.74, 14.73) * mm, "end": v(-10.93, 14.56) * mm});
            skLineSegment(sketch, "E390", {"start": v(-10.93, 14.56) * mm, "end": v(-11, 14.5) * mm});
            skLineSegment(sketch, "E391", {"start": v(-11, 14.5) * mm, "end": v(-11.03, 14.5) * mm});
            skLineSegment(sketch, "E392", {"start": v(-11.03, 14.5) * mm, "end": v(-11.04, 14.5) * mm});
            skLineSegment(sketch, "E393", {"start": v(-11.04, 14.5) * mm, "end": v(-11.05, 14.52) * mm});
            skLineSegment(sketch, "E394", {"start": v(-11.05, 14.52) * mm, "end": v(-11.05, 14.56) * mm});
            skLineSegment(sketch, "E395", {"start": v(-11.05, 14.56) * mm, "end": v(-11.03, 14.66) * mm});
            skLineSegment(sketch, "E396", {"start": v(-11.03, 14.66) * mm, "end": v(-10.95, 14.96) * mm});
            skLineSegment(sketch, "E397", {"start": v(-10.2, 15.58) * mm, "end": v(-9.54, 16.07) * mm});
            skLineSegment(sketch, "E398", {"start": v(-9.54, 16.07) * mm, "end": v(-8.88, 16.46) * mm});
            skLineSegment(sketch, "E399", {"start": v(-8.88, 16.46) * mm, "end": v(-8.35, 16.7) * mm});
            skLineSegment(sketch, "E400", {"start": v(-8.35, 16.7) * mm, "end": v(-7.8, 16.87) * mm});
            skLineSegment(sketch, "E401", {"start": v(-7.8, 16.87) * mm, "end": v(-7.52, 16.92) * mm});
            skLineSegment(sketch, "E402", {"start": v(-7.52, 16.92) * mm, "end": v(-7.16, 16.95) * mm});
            skLineSegment(sketch, "E403", {"start": v(-7.16, 16.95) * mm, "end": v(-6.78, 16.96) * mm});
            skLineSegment(sketch, "E404", {"start": v(-6.78, 16.96) * mm, "end": v(-6.36, 16.94) * mm});
            skLineSegment(sketch, "E405", {"start": v(-6.36, 16.94) * mm, "end": v(-6.03, 16.9) * mm});
            skLineSegment(sketch, "E406", {"start": v(-5.63, 13.32) * mm, "end": v(-5.46, 12.46) * mm});
            skLineSegment(sketch, "E407", {"start": v(-5.46, 12.46) * mm, "end": v(-5.4, 12.25) * mm});
            skArc(sketch, "E408", {"start": v(-5.13, 10.8) * mm, "mid": v(-5.24, 11.53) * mm, "end": v(-5.4, 12.25) * mm});
            skLineSegment(sketch, "E409", {"start": v(-5.13, 10.8) * mm, "end": v(-5.1, 9.92) * mm});
            skLineSegment(sketch, "E410", {"start": v(-5.1, 9.92) * mm, "end": v(-5.1, 9.42) * mm});
            skLineSegment(sketch, "E411", {"start": v(-5.1, 9.42) * mm, "end": v(-5.12, 9.4) * mm});
            skLineSegment(sketch, "E412", {"start": v(-5.12, 9.4) * mm, "end": v(-5.12, 9.38) * mm});
            skLineSegment(sketch, "E413", {"start": v(-5.12, 9.38) * mm, "end": v(-5.12, 9.38) * mm});
            skLineSegment(sketch, "E414", {"start": v(-5.12, 9.38) * mm, "end": v(-5.14, 9.4) * mm});
            skLineSegment(sketch, "E415", {"start": v(-5.14, 9.4) * mm, "end": v(-5.16, 9.42) * mm});
            skLineSegment(sketch, "E416", {"start": v(-5.16, 9.42) * mm, "end": v(-5.2, 9.52) * mm});
            skArc(sketch, "E417", {"start": v(-5.2, 9.52) * mm, "mid": v(-5.33, 9.82) * mm, "end": v(-5.47, 10.12) * mm});
            skLineSegment(sketch, "E418", {"start": v(-5.47, 10.12) * mm, "end": v(-5.61, 10.4) * mm});
            skLineSegment(sketch, "E419", {"start": v(-5.61, 10.4) * mm, "end": v(-5.73, 10.6) * mm});
            skLineSegment(sketch, "E420", {"start": v(-5.73, 10.6) * mm, "end": v(-5.86, 10.76) * mm});
            skLineSegment(sketch, "E421", {"start": v(-5.86, 10.76) * mm, "end": v(-5.9, 10.78) * mm});
            skLineSegment(sketch, "E422", {"start": v(-5.9, 10.78) * mm, "end": v(-5.93, 10.76) * mm});
            skLineSegment(sketch, "E423", {"start": v(-5.93, 10.76) * mm, "end": v(-5.99, 10.64) * mm});
            skLineSegment(sketch, "E424", {"start": v(-5.99, 10.64) * mm, "end": v(-6.03, 10.47) * mm});
            skLineSegment(sketch, "E425", {"start": v(-6.03, 10.47) * mm, "end": v(-6.1, 10.07) * mm});
            skLineSegment(sketch, "E426", {"start": v(-6.1, 10.07) * mm, "end": v(-6.13, 9.7) * mm});
            skLineSegment(sketch, "E427", {"start": v(-6.13, 9.7) * mm, "end": v(-6.12, 9.37) * mm});
            skLineSegment(sketch, "E428", {"start": v(-6.12, 9.37) * mm, "end": v(-6.1, 9.1) * mm});
            skLineSegment(sketch, "E429", {"start": v(-6.1, 9.1) * mm, "end": v(-6.03, 9.3) * mm});
            skLineSegment(sketch, "E430", {"start": v(-6.03, 9.3) * mm, "end": v(-5.92, 9.55) * mm});
            skLineSegment(sketch, "E431", {"start": v(-5.92, 9.55) * mm, "end": v(-5.82, 9.62) * mm});
            skLineSegment(sketch, "E432", {"start": v(-5.82, 9.62) * mm, "end": v(-5.7, 9.59) * mm});
            skLineSegment(sketch, "E433", {"start": v(-5.7, 9.59) * mm, "end": v(-5.6, 9.42) * mm});
            skLineSegment(sketch, "E434", {"start": v(-5.6, 9.42) * mm, "end": v(-5.48, 9.15) * mm});
            skLineSegment(sketch, "E435", {"start": v(-5.48, 9.15) * mm, "end": v(-5.4, 8.86) * mm});
            skLineSegment(sketch, "E436", {"start": v(-5.4, 8.86) * mm, "end": v(-5.38, 8.59) * mm});
            skLineSegment(sketch, "E437", {"start": v(-5.38, 8.59) * mm, "end": v(-5.36, 8.25) * mm});
            skLineSegment(sketch, "E438", {"start": v(-5.36, 8.25) * mm, "end": v(-5.35, 7.88) * mm});
            skLineSegment(sketch, "E439", {"start": v(-5.35, 7.88) * mm, "end": v(-5.37, 7.65) * mm});
            skLineSegment(sketch, "E440", {"start": v(-5.37, 7.65) * mm, "end": v(-5.43, 7.53) * mm});
            skLineSegment(sketch, "E441", {"start": v(-5.43, 7.53) * mm, "end": v(-5.52, 7.5) * mm});
            skLineSegment(sketch, "E442", {"start": v(-5.52, 7.5) * mm, "end": v(-5.7, 7.55) * mm});
            skLineSegment(sketch, "E443", {"start": v(-5.7, 7.55) * mm, "end": v(-5.85, 7.65) * mm});
            skLineSegment(sketch, "E444", {"start": v(-5.85, 7.65) * mm, "end": v(-5.89, 7.69) * mm});
            skLineSegment(sketch, "E445", {"start": v(-5.89, 7.69) * mm, "end": v(-5.9, 7.7) * mm});
            skLineSegment(sketch, "E446", {"start": v(-5.9, 7.7) * mm, "end": v(-5.92, 7.7) * mm});
            skLineSegment(sketch, "E447", {"start": v(-5.92, 7.7) * mm, "end": v(-5.92, 7.7) * mm});
            skLineSegment(sketch, "E448", {"start": v(-5.92, 7.7) * mm, "end": v(-5.9, 7.65) * mm});
            skLineSegment(sketch, "E449", {"start": v(-5.9, 7.65) * mm, "end": v(-5.88, 7.6) * mm});
            skLineSegment(sketch, "E450", {"start": v(-5.88, 7.6) * mm, "end": v(-5.8, 7.44) * mm});
            skLineSegment(sketch, "E451", {"start": v(-5.8, 7.44) * mm, "end": v(-5.65, 7.22) * mm});
            skLineSegment(sketch, "E452", {"start": v(-5.65, 7.22) * mm, "end": v(-5.52, 7.05) * mm});
            skLineSegment(sketch, "E453", {"start": v(-5.52, 7.05) * mm, "end": v(-5.34, 6.9) * mm});
            skLineSegment(sketch, "E454", {"start": v(-5.34, 6.9) * mm, "end": v(-5.27, 6.86) * mm});
            skLineSegment(sketch, "E455", {"start": v(-5.27, 6.86) * mm, "end": v(-5.23, 6.86) * mm});
            skLineSegment(sketch, "E456", {"start": v(-5.23, 6.86) * mm, "end": v(-5.17, 6.9) * mm});
            skLineSegment(sketch, "E457", {"start": v(-5.17, 6.9) * mm, "end": v(-5.17, 6.9) * mm});
            skLineSegment(sketch, "E458", {"start": v(-5.17, 6.9) * mm, "end": v(-5.17, 6.91) * mm});
            skLineSegment(sketch, "E459", {"start": v(-5.17, 6.91) * mm, "end": v(-5.16, 6.93) * mm});
            skLineSegment(sketch, "E460", {"start": v(-5.16, 6.93) * mm, "end": v(-5.14, 7) * mm});
            skLineSegment(sketch, "E461", {"start": v(-5.14, 7) * mm, "end": v(-5.1, 7.18) * mm});
            skLineSegment(sketch, "E462", {"start": v(-5.1, 7.18) * mm, "end": v(-5.06, 7.42) * mm});
            skLineSegment(sketch, "E463", {"start": v(-5.06, 7.42) * mm, "end": v(-5, 7.7) * mm});
            skLineSegment(sketch, "E464", {"start": v(-5, 7.7) * mm, "end": v(-4.9, 8.28) * mm});
            skLineSegment(sketch, "E465", {"start": v(-4.9, 8.28) * mm, "end": v(-4.78, 8.93) * mm});
            skLineSegment(sketch, "E466", {"start": v(-4.78, 8.93) * mm, "end": v(-4.68, 9.5) * mm});
            skLineSegment(sketch, "E467", {"start": v(-4.68, 9.5) * mm, "end": v(-4.6, 10.01) * mm});
            skLineSegment(sketch, "E468", {"start": v(-4.6, 10.01) * mm, "end": v(-4.53, 10.43) * mm});
            skLineSegment(sketch, "E469", {"start": v(-4.53, 10.43) * mm, "end": v(-4.5, 10.7) * mm});
            skLineSegment(sketch, "E470", {"start": v(-4.5, 10.7) * mm, "end": v(-4.5, 11.01) * mm});
            skLineSegment(sketch, "E471", {"start": v(-4.5, 11.01) * mm, "end": v(-4.52, 11.41) * mm});
            skLineSegment(sketch, "E472", {"start": v(-4.52, 11.41) * mm, "end": v(-4.63, 12.07) * mm});
            skLineSegment(sketch, "E473", {"start": v(-4.63, 12.07) * mm, "end": v(-4.5, 11.71) * mm});
            skLineSegment(sketch, "E474", {"start": v(-4.5, 11.71) * mm, "end": v(-4.5, 11.67) * mm});
            skLineSegment(sketch, "E475", {"start": v(-4.5, 11.67) * mm, "end": v(-4.46, 11.57) * mm});
            skLineSegment(sketch, "E476", {"start": v(-4.46, 11.57) * mm, "end": v(-4.36, 11.3) * mm});
            skLineSegment(sketch, "E477", {"start": v(-4.36, 11.3) * mm, "end": v(-4.02, 10.38) * mm});
            skLineSegment(sketch, "E478", {"start": v(-4.02, 10.38) * mm, "end": v(-3.73, 9.49) * mm});
            skLineSegment(sketch, "E479", {"start": v(-3.73, 9.49) * mm, "end": v(-3.55, 8.86) * mm});
            skLineSegment(sketch, "E480", {"start": v(-3.55, 8.86) * mm, "end": v(-3.41, 8.32) * mm});
            skLineSegment(sketch, "E481", {"start": v(-3.41, 8.32) * mm, "end": v(-3.33, 7.82) * mm});
            skLineSegment(sketch, "E482", {"start": v(-3.33, 7.82) * mm, "end": v(-3.28, 7.25) * mm});
            skLineSegment(sketch, "E483", {"start": v(-3.28, 7.25) * mm, "end": v(-3.26, 6.8) * mm});
            skLineSegment(sketch, "E484", {"start": v(-3.26, 6.8) * mm, "end": v(-3.27, 6.4) * mm});
            skLineSegment(sketch, "E485", {"start": v(-3.27, 6.4) * mm, "end": v(-3.28, 6.12) * mm});
            skLineSegment(sketch, "E486", {"start": v(-3.28, 6.12) * mm, "end": v(-3.3, 5.93) * mm});
            skLineSegment(sketch, "E487", {"start": v(-3.3, 5.93) * mm, "end": v(-3.32, 5.83) * mm});
            skLineSegment(sketch, "E488", {"start": v(-3.32, 5.83) * mm, "end": v(-3.34, 5.78) * mm});
            skLineSegment(sketch, "E489", {"start": v(-3.34, 5.78) * mm, "end": v(-3.37, 5.77) * mm});
            skLineSegment(sketch, "E490", {"start": v(-3.37, 5.77) * mm, "end": v(-3.4, 5.77) * mm});
            skLineSegment(sketch, "E491", {"start": v(-3.4, 5.77) * mm, "end": v(-3.51, 5.86) * mm});
            skLineSegment(sketch, "E492", {"start": v(-3.51, 5.86) * mm, "end": v(-3.57, 5.91) * mm});
            skLineSegment(sketch, "E493", {"start": v(-3.57, 5.91) * mm, "end": v(-3.6, 5.92) * mm});
            skLineSegment(sketch, "E494", {"start": v(-3.6, 5.92) * mm, "end": v(-3.6, 5.92) * mm});
            skLineSegment(sketch, "E495", {"start": v(-3.6, 5.92) * mm, "end": v(-3.62, 5.88) * mm});
            skLineSegment(sketch, "E496", {"start": v(-3.62, 5.88) * mm, "end": v(-3.61, 5.78) * mm});
            skLineSegment(sketch, "E497", {"start": v(-3.61, 5.78) * mm, "end": v(-3.58, 5.67) * mm});
            skLineSegment(sketch, "E498", {"start": v(-3.58, 5.67) * mm, "end": v(-3.51, 5.54) * mm});
            skLineSegment(sketch, "E499", {"start": v(-3.51, 5.54) * mm, "end": v(-3.36, 5.32) * mm});
            skLineSegment(sketch, "E500", {"start": v(-3.36, 5.32) * mm, "end": v(-3.2, 5.16) * mm});
            skLineSegment(sketch, "E501", {"start": v(-3.2, 5.16) * mm, "end": v(-3.1, 5.11) * mm});
            skLineSegment(sketch, "E502", {"start": v(-3.1, 5.11) * mm, "end": v(-2.98, 5.17) * mm});
            skLineSegment(sketch, "E503", {"start": v(-2.98, 5.17) * mm, "end": v(-2.86, 5.28) * mm});
            skLineSegment(sketch, "E504", {"start": v(-2.86, 5.28) * mm, "end": v(-2.68, 5.53) * mm});
            skLineSegment(sketch, "E505", {"start": v(-2.68, 5.53) * mm, "end": v(-2.5, 5.8) * mm});
            skLineSegment(sketch, "E506", {"start": v(-2.5, 5.8) * mm, "end": v(-2.41, 5.91) * mm});
            skLineSegment(sketch, "E507", {"start": v(-2.41, 5.91) * mm, "end": v(-2.32, 6.02) * mm});
            skLineSegment(sketch, "E508", {"start": v(-2.32, 6.02) * mm, "end": v(-2.17, 6.2) * mm});
            skLineSegment(sketch, "E509", {"start": v(-2.17, 6.2) * mm, "end": v(-2.07, 6.37) * mm});
            skLineSegment(sketch, "E510", {"start": v(-2.07, 6.37) * mm, "end": v(-1.98, 6.63) * mm});
            skLineSegment(sketch, "E511", {"start": v(-1.98, 6.63) * mm, "end": v(-1.89, 7.02) * mm});
            skLineSegment(sketch, "E512", {"start": v(-1.89, 7.02) * mm, "end": v(-1.8, 7.42) * mm});
            skLineSegment(sketch, "E513", {"start": v(-1.8, 7.42) * mm, "end": v(-1.73, 7.88) * mm});
            skLineSegment(sketch, "E514", {"start": v(-1.73, 7.88) * mm, "end": v(-1.64, 8.52) * mm});
            skLineSegment(sketch, "E515", {"start": v(-1.64, 8.52) * mm, "end": v(-1.58, 9.1) * mm});
            skLineSegment(sketch, "E516", {"start": v(-1.58, 9.1) * mm, "end": v(-1.55, 9.59) * mm});
            skLineSegment(sketch, "E517", {"start": v(-1.55, 9.59) * mm, "end": v(-1.5, 10.1) * mm});
            skLineSegment(sketch, "E518", {"start": v(2.62, 13.91) * mm, "end": v(3.01, 13.9) * mm});
            skLineSegment(sketch, "E519", {"start": v(3.01, 13.9) * mm, "end": v(3.29, 13.84) * mm});
            skLineSegment(sketch, "E520", {"start": v(3.29, 13.84) * mm, "end": v(4.06, 13.55) * mm});
            skLineSegment(sketch, "E521", {"start": v(4.06, 13.55) * mm, "end": v(4.74, 13.14) * mm});
            skLineSegment(sketch, "E522", {"start": v(4.74, 13.14) * mm, "end": v(5.34, 12.59) * mm});
            skLineSegment(sketch, "E523", {"start": v(5.34, 12.59) * mm, "end": v(5.76, 12.05) * mm});
            skLineSegment(sketch, "E524", {"start": v(5.76, 12.05) * mm, "end": v(6.13, 11.41) * mm});
            skLineSegment(sketch, "E525", {"start": v(6.13, 11.41) * mm, "end": v(6.46, 10.68) * mm});
            skLineSegment(sketch, "E526", {"start": v(6.46, 10.68) * mm, "end": v(6.63, 10.25) * mm});
            skLineSegment(sketch, "E527", {"start": v(6.63, 10.25) * mm, "end": v(6.8, 9.73) * mm});
            skLineSegment(sketch, "E528", {"start": v(6.8, 9.73) * mm, "end": v(6.91, 9.35) * mm});
            skLineSegment(sketch, "E529", {"start": v(6.91, 9.35) * mm, "end": v(6.99, 9.05) * mm});
            skLineSegment(sketch, "E530", {"start": v(6.99, 9.05) * mm, "end": v(7.04, 8.85) * mm});
            skLineSegment(sketch, "E531", {"start": v(7.04, 8.85) * mm, "end": v(7.06, 8.8) * mm});
            skLineSegment(sketch, "E532", {"start": v(7.06, 8.8) * mm, "end": v(7.07, 8.79) * mm});
            skLineSegment(sketch, "E533", {"start": v(7.07, 8.79) * mm, "end": v(7.09, 8.78) * mm});
            skLineSegment(sketch, "E534", {"start": v(7.09, 8.78) * mm, "end": v(7.1, 8.79) * mm});
            skLineSegment(sketch, "E535", {"start": v(7.1, 8.79) * mm, "end": v(7.13, 8.86) * mm});
            skLineSegment(sketch, "E536", {"start": v(7.13, 8.86) * mm, "end": v(7.25, 9.3) * mm});
            skLineSegment(sketch, "E537", {"start": v(7.25, 9.3) * mm, "end": v(7.32, 9.9) * mm});
            skLineSegment(sketch, "E538", {"start": v(7.32, 9.9) * mm, "end": v(7.34, 10.6) * mm});
            skLineSegment(sketch, "E539", {"start": v(7.34, 10.6) * mm, "end": v(7.31, 11.5) * mm});
            skLineSegment(sketch, "E540", {"start": v(7.31, 11.5) * mm, "end": v(7.22, 12.42) * mm});
            skLineSegment(sketch, "E541", {"start": v(7.22, 12.42) * mm, "end": v(7.14, 12.9) * mm});
            skLineSegment(sketch, "E542", {"start": v(7.14, 12.9) * mm, "end": v(7.05, 13.28) * mm});
            skLineSegment(sketch, "E543", {"start": v(7.05, 13.28) * mm, "end": v(6.92, 13.61) * mm});
            skLineSegment(sketch, "E544", {"start": v(6.92, 13.61) * mm, "end": v(6.72, 13.99) * mm});
            skLineSegment(sketch, "E545", {"start": v(6.72, 13.99) * mm, "end": v(6.43, 14.4) * mm});
            skLineSegment(sketch, "E546", {"start": v(6.43, 14.4) * mm, "end": v(6.21, 14.7) * mm});
            skLineSegment(sketch, "E547", {"start": v(6.21, 14.7) * mm, "end": v(6.14, 14.82) * mm});
            skLineSegment(sketch, "E548", {"start": v(6.14, 14.82) * mm, "end": v(6.13, 14.83) * mm});
            skLineSegment(sketch, "E549", {"start": v(6.13, 14.83) * mm, "end": v(6.13, 14.83) * mm});
            skLineSegment(sketch, "E550", {"start": v(6.13, 14.83) * mm, "end": v(6.14, 14.83) * mm});
            skLineSegment(sketch, "E551", {"start": v(6.14, 14.83) * mm, "end": v(6.14, 14.83) * mm});
            skLineSegment(sketch, "E552", {"start": v(6.14, 14.83) * mm, "end": v(6.15, 14.83) * mm});
            skLineSegment(sketch, "E553", {"start": v(6.15, 14.83) * mm, "end": v(6.19, 14.8) * mm});
            skLineSegment(sketch, "E554", {"start": v(6.19, 14.8) * mm, "end": v(6.3, 14.7) * mm});
            skLineSegment(sketch, "E555", {"start": v(6.3, 14.7) * mm, "end": v(6.47, 14.53) * mm});
            skLineSegment(sketch, "E556", {"start": v(6.47, 14.53) * mm, "end": v(6.66, 14.34) * mm});
            skLineSegment(sketch, "E557", {"start": v(6.66, 14.34) * mm, "end": v(6.88, 14.1) * mm});
            skLineSegment(sketch, "E558", {"start": v(6.88, 14.1) * mm, "end": v(7.08, 13.89) * mm});
            skLineSegment(sketch, "E559", {"start": v(7.08, 13.89) * mm, "end": v(7.2, 13.75) * mm});
            skLineSegment(sketch, "E560", {"start": v(7.2, 13.75) * mm, "end": v(7.28, 13.65) * mm});
            skLineSegment(sketch, "E561", {"start": v(7.28, 13.65) * mm, "end": v(7.38, 13.52) * mm});
            skLineSegment(sketch, "E562", {"start": v(7.38, 13.52) * mm, "end": v(7.43, 13.46) * mm});
            skLineSegment(sketch, "E563", {"start": v(7.43, 13.46) * mm, "end": v(7.44, 13.45) * mm});
            skLineSegment(sketch, "E564", {"start": v(7.44, 13.45) * mm, "end": v(7.45, 13.46) * mm});
            skLineSegment(sketch, "E565", {"start": v(7.45, 13.46) * mm, "end": v(7.45, 13.46) * mm});
            skLineSegment(sketch, "E566", {"start": v(7.45, 13.46) * mm, "end": v(7.45, 13.47) * mm});
            skLineSegment(sketch, "E567", {"start": v(7.45, 13.47) * mm, "end": v(7.45, 13.48) * mm});
            skLineSegment(sketch, "E568", {"start": v(7.45, 13.48) * mm, "end": v(7.44, 13.52) * mm});
            skLineSegment(sketch, "E569", {"start": v(7.44, 13.52) * mm, "end": v(7.42, 13.61) * mm});
            skLineSegment(sketch, "E570", {"start": v(7.42, 13.61) * mm, "end": v(7.34, 13.86) * mm});
            skLineSegment(sketch, "E571", {"start": v(7.34, 13.86) * mm, "end": v(7.25, 14.14) * mm});
            skLineSegment(sketch, "E572", {"start": v(7.25, 14.14) * mm, "end": v(7.14, 14.46) * mm});
            skLineSegment(sketch, "E573", {"start": v(7.14, 14.46) * mm, "end": v(7, 14.84) * mm});
            skLineSegment(sketch, "E574", {"start": v(7, 14.84) * mm, "end": v(6.87, 15.19) * mm});
            skLineSegment(sketch, "E575", {"start": v(6.87, 15.19) * mm, "end": v(6.76, 15.45) * mm});
            skLineSegment(sketch, "E576", {"start": v(6.76, 15.45) * mm, "end": v(6.39, 16.17) * mm});
            skLineSegment(sketch, "E577", {"start": v(6.39, 16.17) * mm, "end": v(6.1, 16.59) * mm});
            skLineSegment(sketch, "E578", {"start": v(6.1, 16.59) * mm, "end": v(5.81, 16.85) * mm});
            skLineSegment(sketch, "E579", {"start": v(5.81, 16.85) * mm, "end": v(5.4, 17.12) * mm});
            skLineSegment(sketch, "E580", {"start": v(5.4, 17.12) * mm, "end": v(4.92, 17.37) * mm});
            skLineSegment(sketch, "E581", {"start": v(4.92, 17.37) * mm, "end": v(4.3, 17.63) * mm});
            skLineSegment(sketch, "E582", {"start": v(4.3, 17.63) * mm, "end": v(3.65, 17.8) * mm});
            skLineSegment(sketch, "E583", {"start": v(3.65, 17.8) * mm, "end": v(3.32, 17.88) * mm});
            skLineSegment(sketch, "E584", {"start": v(3.32, 17.88) * mm, "end": v(3.9, 17.87) * mm});
            skLineSegment(sketch, "E585", {"start": v(3.9, 17.87) * mm, "end": v(4.49, 17.82) * mm});
            skLineSegment(sketch, "E586", {"start": v(4.49, 17.82) * mm, "end": v(5.01, 17.72) * mm});
            skLineSegment(sketch, "E587", {"start": v(5.01, 17.72) * mm, "end": v(5.42, 17.58) * mm});
            skLineSegment(sketch, "E588", {"start": v(5.42, 17.58) * mm, "end": v(5.84, 17.39) * mm});
            skLineSegment(sketch, "E589", {"start": v(5.84, 17.39) * mm, "end": v(6.02, 17.3) * mm});
            skLineSegment(sketch, "E590", {"start": v(6.02, 17.3) * mm, "end": v(6.13, 17.27) * mm});
            skLineSegment(sketch, "E591", {"start": v(6.13, 17.27) * mm, "end": v(6.15, 17.26) * mm});
            skLineSegment(sketch, "E592", {"start": v(6.15, 17.26) * mm, "end": v(6.15, 17.27) * mm});
            skLineSegment(sketch, "E593", {"start": v(6.15, 17.27) * mm, "end": v(6.16, 17.27) * mm});
            skLineSegment(sketch, "E594", {"start": v(6.16, 17.27) * mm, "end": v(6.15, 17.3) * mm});
            skLineSegment(sketch, "E595", {"start": v(6.15, 17.3) * mm, "end": v(6.13, 17.35) * mm});
            skLineSegment(sketch, "E596", {"start": v(6.13, 17.35) * mm, "end": v(6.09, 17.47) * mm});
            skLineSegment(sketch, "E597", {"start": v(6.09, 17.47) * mm, "end": v(5.96, 17.76) * mm});
            skLineSegment(sketch, "E598", {"start": v(5.96, 17.76) * mm, "end": v(5.68, 18.37) * mm});
            skLineSegment(sketch, "E599", {"start": v(5.68, 18.37) * mm, "end": v(5.32, 19) * mm});
            skLineSegment(sketch, "E600", {"start": v(5.32, 19) * mm, "end": v(4.96, 19.5) * mm});
            skLineSegment(sketch, "E601", {"start": v(4.96, 19.5) * mm, "end": v(4.68, 19.8) * mm});
            skLineSegment(sketch, "E602", {"start": v(4.68, 19.8) * mm, "end": v(4.4, 20) * mm});
            skLineSegment(sketch, "E603", {"start": v(4.4, 20) * mm, "end": v(3.9, 20.19) * mm});
            skLineSegment(sketch, "E604", {"start": v(3.9, 20.19) * mm, "end": v(3.4, 20.26) * mm});
            skLineSegment(sketch, "E605", {"start": v(3.4, 20.26) * mm, "end": v(3.06, 20.28) * mm});
            skLineSegment(sketch, "E606", {"start": v(3.06, 20.28) * mm, "end": v(3.26, 20.33) * mm});
            skArc(sketch, "E607", {"start": v(3.98, 20.44) * mm, "mid": v(3.62, 20.39) * mm, "end": v(3.26, 20.33) * mm});
            skLineSegment(sketch, "E608", {"start": v(3.98, 20.44) * mm, "end": v(4.5, 20.5) * mm});
            skLineSegment(sketch, "E609", {"start": v(4.5, 20.5) * mm, "end": v(4.4, 20.58) * mm});
            skLineSegment(sketch, "E610", {"start": v(4.4, 20.58) * mm, "end": v(4.19, 20.72) * mm});
            skLineSegment(sketch, "E611", {"start": v(4.19, 20.72) * mm, "end": v(3.9, 20.86) * mm});
            skLineSegment(sketch, "E612", {"start": v(3.9, 20.86) * mm, "end": v(3.67, 20.96) * mm});
            skLineSegment(sketch, "E613", {"start": v(3.67, 20.96) * mm, "end": v(3.46, 21.03) * mm});
            skLineSegment(sketch, "E614", {"start": v(3.46, 21.03) * mm, "end": v(3.26, 21.08) * mm});
            skLineSegment(sketch, "E615", {"start": v(3.26, 21.08) * mm, "end": v(3.05, 21.1) * mm});
            skLineSegment(sketch, "E616", {"start": v(3.05, 21.1) * mm, "end": v(2.82, 21.12) * mm});
            skLineSegment(sketch, "E617", {"start": v(2.82, 21.12) * mm, "end": v(2.48, 21.12) * mm});
            skLineSegment(sketch, "E618", {"start": v(2.48, 21.12) * mm, "end": v(2.12, 21.11) * mm});
            skLineSegment(sketch, "E619", {"start": v(2.12, 21.11) * mm, "end": v(1.84, 21.1) * mm});
            skLineSegment(sketch, "E620", {"start": v(1.84, 21.1) * mm, "end": v(1.6, 21.06) * mm});
            skLineSegment(sketch, "E621", {"start": v(1.6, 21.06) * mm, "end": v(1.16, 20.9) * mm});
            skLineSegment(sketch, "E622", {"start": v(1.16, 20.9) * mm, "end": v(0.92, 20.75) * mm});
            skLineSegment(sketch, "E623", {"start": v(0.92, 20.75) * mm, "end": v(0.64, 20.53) * mm});
            skLineSegment(sketch, "E624", {"start": v(0.64, 20.53) * mm, "end": v(0.23, 20.13) * mm});
            skLineSegment(sketch, "E625", {"start": v(0.23, 20.13) * mm, "end": v(0, 19.9) * mm});
            skLineSegment(sketch, "E626", {"start": v(0, 19.9) * mm, "end": v(-0.01, 19.89) * mm});
            skLineSegment(sketch, "E627", {"start": v(-0.01, 19.89) * mm, "end": v(-0.02, 19.88) * mm});
            skLineSegment(sketch, "E628", {"start": v(-0.02, 19.88) * mm, "end": v(-0.02, 19.88) * mm});
            skLineSegment(sketch, "E629", {"start": v(-0.02, 19.88) * mm, "end": v(-0.02, 19.9) * mm});
            skLineSegment(sketch, "E630", {"start": v(-0.02, 19.9) * mm, "end": v(-0.01, 19.92) * mm});
            skLineSegment(sketch, "E631", {"start": v(-0.01, 19.92) * mm, "end": v(0.02, 19.99) * mm});
            skLineSegment(sketch, "E632", {"start": v(0.02, 19.99) * mm, "end": v(0.17, 20.2) * mm});
            skLineSegment(sketch, "E633", {"start": v(0.17, 20.2) * mm, "end": v(0.57, 20.72) * mm});
            skArc(sketch, "E634", {"start": v(2.55, 21.93) * mm, "mid": v(1.46, 21.48) * mm, "end": v(0.57, 20.72) * mm});
            skArc(sketch, "E635", {"start": v(3.15, 22.06) * mm, "mid": v(2.85, 22) * mm, "end": v(2.55, 21.93) * mm});
            skLineSegment(sketch, "E636", {"start": v(3.15, 22.06) * mm, "end": v(3.28, 22.09) * mm});
            skLineSegment(sketch, "E637", {"start": v(3.28, 22.09) * mm, "end": v(3.32, 22.1) * mm});
            skLineSegment(sketch, "E638", {"start": v(3.32, 22.1) * mm, "end": v(3.33, 22.11) * mm});
            skLineSegment(sketch, "E639", {"start": v(3.33, 22.11) * mm, "end": v(3.33, 22.12) * mm});
            skLineSegment(sketch, "E640", {"start": v(3.33, 22.12) * mm, "end": v(3.33, 22.12) * mm});
            skLineSegment(sketch, "E641", {"start": v(3.33, 22.12) * mm, "end": v(3.33, 22.13) * mm});
            skLineSegment(sketch, "E642", {"start": v(3.33, 22.13) * mm, "end": v(3.3, 22.14) * mm});
            skLineSegment(sketch, "E643", {"start": v(3.3, 22.14) * mm, "end": v(3.24, 22.18) * mm});
            skLineSegment(sketch, "E644", {"start": v(3.24, 22.18) * mm, "end": v(3, 22.32) * mm});
            skLineSegment(sketch, "E645", {"start": v(3, 22.32) * mm, "end": v(2.64, 22.5) * mm});
            skLineSegment(sketch, "E646", {"start": v(2.64, 22.5) * mm, "end": v(2.23, 22.7) * mm});
            skLineSegment(sketch, "E647", {"start": v(2.23, 22.7) * mm, "end": v(1.77, 22.92) * mm});
            skLineSegment(sketch, "E648", {"start": v(1.77, 22.92) * mm, "end": v(1.38, 23.1) * mm});
            skLineSegment(sketch, "E649", {"start": v(1.38, 23.1) * mm, "end": v(1.14, 23.2) * mm});
            skLineSegment(sketch, "E650", {"start": v(1.14, 23.2) * mm, "end": v(1.07, 23.23) * mm});
            skLineSegment(sketch, "E651", {"start": v(1.07, 23.23) * mm, "end": v(1.05, 23.23) * mm});
            skLineSegment(sketch, "E652", {"start": v(1.05, 23.23) * mm, "end": v(0.85, 23.18) * mm});
            skLineSegment(sketch, "E653", {"start": v(0.85, 23.18) * mm, "end": v(0.6, 23.04) * mm});
            skLineSegment(sketch, "E654", {"start": v(0.6, 23.04) * mm, "end": v(0.36, 22.86) * mm});
            skLineSegment(sketch, "E655", {"start": v(0.36, 22.86) * mm, "end": v(0.1, 22.62) * mm});
            skLineSegment(sketch, "E656", {"start": v(0.1, 22.62) * mm, "end": v(-0.12, 22.43) * mm});
            skLineSegment(sketch, "E657", {"start": v(-0.12, 22.43) * mm, "end": v(-0.14, 22.42) * mm});
            skLineSegment(sketch, "E658", {"start": v(-0.14, 22.42) * mm, "end": v(-0.14, 22.42) * mm});
            skLineSegment(sketch, "E659", {"start": v(-0.14, 22.42) * mm, "end": v(-0.14, 22.43) * mm});
            skLineSegment(sketch, "E660", {"start": v(-0.14, 22.43) * mm, "end": v(-0.13, 22.45) * mm});
            skLineSegment(sketch, "E661", {"start": v(-0.13, 22.45) * mm, "end": v(-0.1, 22.5) * mm});
            skLineSegment(sketch, "E662", {"start": v(-0.1, 22.5) * mm, "end": v(-0.03, 22.61) * mm});
            skLineSegment(sketch, "E663", {"start": v(-0.03, 22.61) * mm, "end": v(0.17, 22.88) * mm});
            skLineSegment(sketch, "E664", {"start": v(0.17, 22.88) * mm, "end": v(0.37, 23.14) * mm});
            skLineSegment(sketch, "E665", {"start": v(0.37, 23.14) * mm, "end": v(0.55, 23.35) * mm});
            skLineSegment(sketch, "E666", {"start": v(0.55, 23.35) * mm, "end": v(0.75, 23.58) * mm});
            skLineSegment(sketch, "E667", {"start": v(0.75, 23.58) * mm, "end": v(0.8, 23.64) * mm});
            skLineSegment(sketch, "E668", {"start": v(0.8, 23.64) * mm, "end": v(0.8, 23.66) * mm});
            skLineSegment(sketch, "E669", {"start": v(0.8, 23.66) * mm, "end": v(0.8, 23.67) * mm});
            skLineSegment(sketch, "E670", {"start": v(0.8, 23.67) * mm, "end": v(0.77, 23.7) * mm});
            skLineSegment(sketch, "E671", {"start": v(0.77, 23.7) * mm, "end": v(0.68, 23.73) * mm});
            skLineSegment(sketch, "E672", {"start": v(0.68, 23.73) * mm, "end": v(0.54, 23.76) * mm});
            skLineSegment(sketch, "E673", {"start": v(0.54, 23.76) * mm, "end": v(0.32, 23.78) * mm});
            skLineSegment(sketch, "E674", {"start": v(0.32, 23.78) * mm, "end": v(-0.05, 23.8) * mm});
            skLineSegment(sketch, "E675", {"start": v(-0.05, 23.8) * mm, "end": v(-0.4, 23.77) * mm});
            skLineSegment(sketch, "E676", {"start": v(-0.4, 23.77) * mm, "end": v(-0.86, 23.64) * mm});
            skLineSegment(sketch, "E677", {"start": v(-0.86, 23.64) * mm, "end": v(-0.97, 23.6) * mm});
            skLineSegment(sketch, "E678", {"start": v(-0.97, 23.6) * mm, "end": v(-1.06, 23.52) * mm});
            skLineSegment(sketch, "E679", {"start": v(-1.06, 23.52) * mm, "end": v(-1.15, 23.37) * mm});
            skLineSegment(sketch, "E680", {"start": v(-1.15, 23.37) * mm, "end": v(-1.25, 23.16) * mm});
            skLineSegment(sketch, "E681", {"start": v(-1.25, 23.16) * mm, "end": v(-1.4, 22.85) * mm});
            skLineSegment(sketch, "E682", {"start": v(-1.4, 22.85) * mm, "end": v(-1.59, 22.4) * mm});
            skLineSegment(sketch, "E683", {"start": v(-1.59, 22.4) * mm, "end": v(-1.81, 21.92) * mm});
            skLineSegment(sketch, "E684", {"start": v(-1.81, 21.92) * mm, "end": v(-1.83, 21.9) * mm});
            skLineSegment(sketch, "E685", {"start": v(-1.83, 21.9) * mm, "end": v(-1.83, 21.9) * mm});
            skLineSegment(sketch, "E686", {"start": v(-1.83, 21.9) * mm, "end": v(-1.83, 21.95) * mm});
            skLineSegment(sketch, "E687", {"start": v(-1.83, 21.95) * mm, "end": v(-1.81, 22.02) * mm});
            skLineSegment(sketch, "E688", {"start": v(-1.81, 22.02) * mm, "end": v(-1.76, 22.2) * mm});
            skLineSegment(sketch, "E689", {"start": v(-1.76, 22.2) * mm, "end": v(-1.64, 22.6) * mm});
            skLineSegment(sketch, "E690", {"start": v(-1.64, 22.6) * mm, "end": v(-1.5, 23) * mm});
            skLineSegment(sketch, "E691", {"start": v(-1.5, 23) * mm, "end": v(-1.39, 23.35) * mm});
            skLineSegment(sketch, "E692", {"start": v(-1.39, 23.35) * mm, "end": v(-1.32, 23.53) * mm});
            skLineSegment(sketch, "E693", {"start": v(-1.32, 23.53) * mm, "end": v(-1.27, 23.67) * mm});
            skLineSegment(sketch, "E694", {"start": v(-1.27, 23.67) * mm, "end": v(-1.25, 23.76) * mm});
            skLineSegment(sketch, "E695", {"start": v(-1.25, 23.76) * mm, "end": v(-1.24, 23.78) * mm});
            skLineSegment(sketch, "E696", {"start": v(-1.24, 23.78) * mm, "end": v(-1.24, 23.78) * mm});
            skLineSegment(sketch, "E697", {"start": v(-1.24, 23.78) * mm, "end": v(-1.25, 23.79) * mm});
            skLineSegment(sketch, "E698", {"start": v(-1.25, 23.79) * mm, "end": v(-1.25, 23.8) * mm});
            skLineSegment(sketch, "E699", {"start": v(-1.25, 23.8) * mm, "end": v(-1.26, 23.8) * mm});
            skLineSegment(sketch, "E700", {"start": v(-1.26, 23.8) * mm, "end": v(-1.29, 23.8) * mm});
            skLineSegment(sketch, "E701", {"start": v(-1.29, 23.8) * mm, "end": v(-1.36, 23.81) * mm});
            skLineSegment(sketch, "E702", {"start": v(-1.36, 23.81) * mm, "end": v(-1.6, 23.81) * mm});
            skLineSegment(sketch, "E703", {"start": v(-1.6, 23.81) * mm, "end": v(-1.86, 23.8) * mm});
            skLineSegment(sketch, "E704", {"start": v(-1.86, 23.8) * mm, "end": v(-2.06, 23.76) * mm});
            skLineSegment(sketch, "E705", {"start": v(-2.06, 23.76) * mm, "end": v(-2.27, 23.64) * mm});
            skLineSegment(sketch, "E706", {"start": v(-2.27, 23.64) * mm, "end": v(-2.42, 23.43) * mm});
            skLineSegment(sketch, "E707", {"start": v(-2.42, 23.43) * mm, "end": v(-2.51, 23.15) * mm});
            skLineSegment(sketch, "E708", {"start": v(-2.51, 23.15) * mm, "end": v(-2.6, 22.74) * mm});
            skLineSegment(sketch, "E709", {"start": v(-2.6, 22.74) * mm, "end": v(-2.67, 22.37) * mm});
            skLineSegment(sketch, "E710", {"start": v(-2.67, 22.37) * mm, "end": v(-2.71, 21.91) * mm});
            skLineSegment(sketch, "E711", {"start": v(-2.71, 21.91) * mm, "end": v(-2.73, 21.6) * mm});
            skLineSegment(sketch, "E712", {"start": v(-2.73, 21.6) * mm, "end": v(-2.72, 21.37) * mm});
            skLineSegment(sketch, "E713", {"start": v(-2.72, 21.37) * mm, "end": v(-2.71, 21.28) * mm});
            skLineSegment(sketch, "E714", {"start": v(-2.71, 21.28) * mm, "end": v(-2.72, 21.26) * mm});
            skLineSegment(sketch, "E715", {"start": v(-2.72, 21.26) * mm, "end": v(-2.72, 21.26) * mm});
            skLineSegment(sketch, "E716", {"start": v(-2.72, 21.26) * mm, "end": v(-2.75, 21.32) * mm});
            skLineSegment(sketch, "E717", {"start": v(-2.75, 21.32) * mm, "end": v(-2.82, 21.5) * mm});
            skLineSegment(sketch, "E718", {"start": v(-2.82, 21.5) * mm, "end": v(-2.9, 21.7) * mm});
            skLineSegment(sketch, "E719", {"start": v(-2.9, 21.7) * mm, "end": v(-2.94, 21.78) * mm});
            skLineSegment(sketch, "E720", {"start": v(-2.94, 21.78) * mm, "end": v(-2.95, 21.78) * mm});
            skLineSegment(sketch, "E721", {"start": v(-2.95, 21.78) * mm, "end": v(-2.96, 21.78) * mm});
            skLineSegment(sketch, "E722", {"start": v(-2.96, 21.78) * mm, "end": v(-2.96, 21.78) * mm});
            skLineSegment(sketch, "E723", {"start": v(-2.96, 21.78) * mm, "end": v(-2.97, 21.74) * mm});
            skLineSegment(sketch, "E724", {"start": v(-2.97, 21.74) * mm, "end": v(-2.98, 21.69) * mm});
            skLineSegment(sketch, "E725", {"start": v(-2.98, 21.69) * mm, "end": v(-2.99, 21.54) * mm});
            skLineSegment(sketch, "E726", {"start": v(-2.99, 21.54) * mm, "end": v(-3, 21.16) * mm});
            skLineSegment(sketch, "E727", {"start": v(-3, 21.16) * mm, "end": v(-2.99, 20.71) * mm});
            skLineSegment(sketch, "E728", {"start": v(-2.99, 20.71) * mm, "end": v(-2.97, 20.22) * mm});
            skLineSegment(sketch, "E729", {"start": v(-2.97, 20.22) * mm, "end": v(-2.95, 19.6) * mm});
            skLineSegment(sketch, "E730", {"start": v(-2.95, 19.6) * mm, "end": v(-2.9, 19.04) * mm});
            skLineSegment(sketch, "E731", {"start": v(-2.9, 19.04) * mm, "end": v(-2.87, 18.59) * mm});
            skLineSegment(sketch, "E732", {"start": v(-2.87, 18.59) * mm, "end": v(-2.84, 18.4) * mm});
            skLineSegment(sketch, "E733", {"start": v(-2.84, 18.4) * mm, "end": v(-2.83, 18.25) * mm});
            skLineSegment(sketch, "E734", {"start": v(-2.83, 18.25) * mm, "end": v(-2.82, 18.17) * mm});
            skLineSegment(sketch, "E735", {"start": v(-2.82, 18.17) * mm, "end": v(-2.82, 18.15) * mm});
            skLineSegment(sketch, "E736", {"start": v(-2.82, 18.15) * mm, "end": v(-2.82, 18.15) * mm});
            skLineSegment(sketch, "E737", {"start": v(-2.82, 18.15) * mm, "end": v(-2.82, 18.14) * mm});
            skLineSegment(sketch, "E738", {"start": v(-2.82, 18.14) * mm, "end": v(-2.82, 18.14) * mm});
            skLineSegment(sketch, "E739", {"start": v(-2.82, 18.14) * mm, "end": v(-2.83, 18.14) * mm});
            skLineSegment(sketch, "E740", {"start": v(-2.83, 18.14) * mm, "end": v(-2.83, 18.16) * mm});
            skLineSegment(sketch, "E741", {"start": v(-2.83, 18.16) * mm, "end": v(-2.9, 18.34) * mm});
            skLineSegment(sketch, "E742", {"start": v(-2.9, 18.34) * mm, "end": v(-3.1, 18.9) * mm});
            skLineSegment(sketch, "E743", {"start": v(-3.1, 18.9) * mm, "end": v(-3.35, 19.52) * mm});
            skLineSegment(sketch, "E744", {"start": v(-3.35, 19.52) * mm, "end": v(-3.64, 20.16) * mm});
            skLineSegment(sketch, "E745", {"start": v(-3.64, 20.16) * mm, "end": v(-3.88, 20.63) * mm});
            skLineSegment(sketch, "E746", {"start": v(-3.88, 20.63) * mm, "end": v(-4.1, 21.06) * mm});
            skLineSegment(sketch, "E747", {"start": v(-4.1, 21.06) * mm, "end": v(-4.32, 21.4) * mm});
            skLineSegment(sketch, "E748", {"start": v(-4.32, 21.4) * mm, "end": v(-4.4, 21.52) * mm});
            skLineSegment(sketch, "E749", {"start": v(-4.4, 21.52) * mm, "end": v(-4.42, 21.53) * mm});
            skLineSegment(sketch, "E750", {"start": v(-4.42, 21.53) * mm, "end": v(-4.43, 21.53) * mm});
            skLineSegment(sketch, "E751", {"start": v(-4.43, 21.53) * mm, "end": v(-4.43, 21.53) * mm});
            skLineSegment(sketch, "E752", {"start": v(-4.43, 21.53) * mm, "end": v(-4.44, 21.51) * mm});
            skLineSegment(sketch, "E753", {"start": v(-4.44, 21.51) * mm, "end": v(-4.44, 21.49) * mm});
            skLineSegment(sketch, "E754", {"start": v(-4.44, 21.49) * mm, "end": v(-4.44, 21.41) * mm});
            skLineSegment(sketch, "E755", {"start": v(-4.44, 21.41) * mm, "end": v(-4.42, 21.28) * mm});
            skLineSegment(sketch, "E756", {"start": v(-4.42, 21.28) * mm, "end": v(-4.4, 21.1) * mm});
            skLineSegment(sketch, "E757", {"start": v(-4.4, 21.1) * mm, "end": v(-4.38, 20.87) * mm});
            skLineSegment(sketch, "E758", {"start": v(-4.38, 20.87) * mm, "end": v(-4.38, 20.8) * mm});
            skLineSegment(sketch, "E759", {"start": v(-4.38, 20.8) * mm, "end": v(-4.38, 20.8) * mm});
            skLineSegment(sketch, "E760", {"start": v(-4.38, 20.8) * mm, "end": v(-4.38, 20.79) * mm});
            skLineSegment(sketch, "E761", {"start": v(-4.38, 20.79) * mm, "end": v(-4.38, 20.79) * mm});
            skLineSegment(sketch, "E762", {"start": v(-4.38, 20.79) * mm, "end": v(-4.4, 20.82) * mm});
            skLineSegment(sketch, "E763", {"start": v(-4.4, 20.82) * mm, "end": v(-4.64, 21.19) * mm});
            skLineSegment(sketch, "E764", {"start": v(-4.64, 21.19) * mm, "end": v(-4.88, 21.57) * mm});
            skLineSegment(sketch, "E765", {"start": v(-4.88, 21.57) * mm, "end": v(-5.05, 21.79) * mm});
            skLineSegment(sketch, "E766", {"start": v(-5.05, 21.79) * mm, "end": v(-5.15, 21.9) * mm});
            skLineSegment(sketch, "E767", {"start": v(-5.15, 21.9) * mm, "end": v(-5.22, 21.95) * mm});
            skLineSegment(sketch, "E768", {"start": v(-5.22, 21.95) * mm, "end": v(-5.35, 21.95) * mm});
            skLineSegment(sketch, "E769", {"start": v(-5.35, 21.95) * mm, "end": v(-5.5, 21.9) * mm});
            skLineSegment(sketch, "E770", {"start": v(-5.5, 21.9) * mm, "end": v(-5.71, 21.83) * mm});
            skLineSegment(sketch, "E771", {"start": v(-5.71, 21.83) * mm, "end": v(-6.16, 21.64) * mm});
            skLineSegment(sketch, "E772", {"start": v(-6.16, 21.64) * mm, "end": v(-6.38, 21.55) * mm});
            skLineSegment(sketch, "E773", {"start": v(-6.38, 21.55) * mm, "end": v(-6.55, 21.47) * mm});
            skLineSegment(sketch, "E774", {"start": v(-6.55, 21.47) * mm, "end": v(-6.66, 21.42) * mm});
            skLineSegment(sketch, "E775", {"start": v(-6.66, 21.42) * mm, "end": v(-6.7, 21.4) * mm});
            skLineSegment(sketch, "E776", {"start": v(-6.7, 21.4) * mm, "end": v(-6.7, 21.39) * mm});
            skLineSegment(sketch, "E777", {"start": v(-6.7, 21.39) * mm, "end": v(-6.7, 21.39) * mm});
            skLineSegment(sketch, "E778", {"start": v(-6.7, 21.39) * mm, "end": v(-6.69, 21.38) * mm});
            skLineSegment(sketch, "E779", {"start": v(-6.69, 21.38) * mm, "end": v(-6.6, 21.33) * mm});
            skLineSegment(sketch, "E780", {"start": v(-6.6, 21.33) * mm, "end": v(-6.5, 21.28) * mm});
            skLineSegment(sketch, "E781", {"start": v(-6.5, 21.28) * mm, "end": v(-5.95, 21.04) * mm});
            skLineSegment(sketch, "E782", {"start": v(-5.95, 21.04) * mm, "end": v(-5.56, 20.8) * mm});
            skLineSegment(sketch, "E783", {"start": v(-5.56, 20.8) * mm, "end": v(-5.42, 20.7) * mm});
            skLineSegment(sketch, "E784", {"start": v(-5.42, 20.7) * mm, "end": v(-5.23, 20.53) * mm});
            skLineSegment(sketch, "E785", {"start": v(-5.23, 20.53) * mm, "end": v(-5.03, 20.35) * mm});
            skLineSegment(sketch, "E786", {"start": v(-5.03, 20.35) * mm, "end": v(-4.88, 20.2) * mm});
            skLineSegment(sketch, "E787", {"start": v(-4.88, 20.2) * mm, "end": v(-4.83, 20.16) * mm});
            skLineSegment(sketch, "E788", {"start": v(-4.83, 20.16) * mm, "end": v(-4.82, 20.14) * mm});
            skLineSegment(sketch, "E789", {"start": v(-4.82, 20.14) * mm, "end": v(-4.82, 20.13) * mm});
            skLineSegment(sketch, "E790", {"start": v(-4.82, 20.13) * mm, "end": v(-4.82, 20.13) * mm});
            skLineSegment(sketch, "E791", {"start": v(-4.82, 20.13) * mm, "end": v(-5.35, 20.38) * mm});
            skLineSegment(sketch, "E792", {"start": v(-5.35, 20.38) * mm, "end": v(-5.79, 20.6) * mm});
            skLineSegment(sketch, "E793", {"start": v(-5.79, 20.6) * mm, "end": v(-6.12, 20.72) * mm});
            skLineSegment(sketch, "E794", {"start": v(-6.12, 20.72) * mm, "end": v(-6.56, 20.8) * mm});
            skLineSegment(sketch, "E795", {"start": v(-6.56, 20.8) * mm, "end": v(-7.07, 20.75) * mm});
            skLineSegment(sketch, "E796", {"start": v(-7.07, 20.75) * mm, "end": v(-7.4, 20.58) * mm});
            skLineSegment(sketch, "E797", {"start": v(-7.4, 20.58) * mm, "end": v(-7.63, 20.35) * mm});
            skLineSegment(sketch, "E798", {"start": v(-7.63, 20.35) * mm, "end": v(-7.94, 20.01) * mm});
            skLineSegment(sketch, "E799", {"start": v(-7.94, 20.01) * mm, "end": v(-8.26, 19.63) * mm});
            skLineSegment(sketch, "E800", {"start": v(-8.26, 19.63) * mm, "end": v(-8.47, 19.35) * mm});
            skLineSegment(sketch, "E801", {"start": v(-8.47, 19.35) * mm, "end": v(-8.65, 19.1) * mm});
            skLineSegment(sketch, "E802", {"start": v(-8.65, 19.1) * mm, "end": v(-8.75, 18.92) * mm});
            skLineSegment(sketch, "E803", {"start": v(-8.75, 18.92) * mm, "end": v(-8.78, 18.87) * mm});
            skLineSegment(sketch, "E804", {"start": v(-8.78, 18.87) * mm, "end": v(-8.78, 18.85) * mm});
            skLineSegment(sketch, "E805", {"start": v(-8.78, 18.85) * mm, "end": v(-8.77, 18.84) * mm});
            skLineSegment(sketch, "E806", {"start": v(-8.77, 18.84) * mm, "end": v(-8.77, 18.84) * mm});
            skLineSegment(sketch, "E807", {"start": v(-8.77, 18.84) * mm, "end": v(-8.76, 18.83) * mm});
            skLineSegment(sketch, "E808", {"start": v(-8.76, 18.83) * mm, "end": v(-8.75, 18.84) * mm});
            skLineSegment(sketch, "E809", {"start": v(-8.75, 18.84) * mm, "end": v(-8.7, 18.84) * mm});
            skLineSegment(sketch, "E810", {"start": v(-8.7, 18.84) * mm, "end": v(-8.6, 18.88) * mm});
            skLineSegment(sketch, "E811", {"start": v(-8.6, 18.88) * mm, "end": v(-8.37, 18.94) * mm});
            skLineSegment(sketch, "E812", {"start": v(-8.37, 18.94) * mm, "end": v(-8.08, 19) * mm});
            skLineSegment(sketch, "E813", {"start": v(-8.08, 19) * mm, "end": v(-7.86, 19.02) * mm});
            skLineSegment(sketch, "E814", {"start": v(-7.86, 19.02) * mm, "end": v(-7.7, 19.04) * mm});
            skLineSegment(sketch, "E815", {"start": v(-7.7, 19.04) * mm, "end": v(-7.63, 19.03) * mm});
            skLineSegment(sketch, "E816", {"start": v(-7.63, 19.03) * mm, "end": v(-7.62, 19.03) * mm});
            skLineSegment(sketch, "E817", {"start": v(-7.62, 19.03) * mm, "end": v(-7.61, 19.03) * mm});
            skLineSegment(sketch, "E818", {"start": v(-7.61, 19.03) * mm, "end": v(-7.61, 19.03) * mm});
            skLineSegment(sketch, "E819", {"start": v(-7.61, 19.03) * mm, "end": v(-7.61, 19.02) * mm});
            skLineSegment(sketch, "E820", {"start": v(-7.61, 19.02) * mm, "end": v(-7.62, 19.02) * mm});
            skLineSegment(sketch, "E821", {"start": v(-7.62, 19.02) * mm, "end": v(-7.78, 18.95) * mm});
            skLineSegment(sketch, "E822", {"start": v(-7.78, 18.95) * mm, "end": v(-8.05, 18.8) * mm});
            skLineSegment(sketch, "E823", {"start": v(-8.05, 18.8) * mm, "end": v(-8.37, 18.61) * mm});
            skLineSegment(sketch, "E824", {"start": v(-8.37, 18.61) * mm, "end": v(-8.6, 18.44) * mm});
            skLineSegment(sketch, "E825", {"start": v(-8.6, 18.44) * mm, "end": v(-8.8, 18.26) * mm});
            skLineSegment(sketch, "E826", {"start": v(-8.8, 18.26) * mm, "end": v(-9.03, 18.04) * mm});
            skLineSegment(sketch, "E827", {"start": v(-9.03, 18.04) * mm, "end": v(-9.24, 17.77) * mm});
            skLineSegment(sketch, "E828", {"start": v(-9.24, 17.77) * mm, "end": v(-9.42, 17.52) * mm});
            skLineSegment(sketch, "E829", {"start": v(-9.42, 17.52) * mm, "end": v(-9.6, 17.21) * mm});
            skLineSegment(sketch, "E830", {"start": v(-9.6, 17.21) * mm, "end": v(-9.81, 16.84) * mm});
            skLineSegment(sketch, "E831", {"start": v(-9.81, 16.84) * mm, "end": v(-10.05, 16.4) * mm});
            skLineSegment(sketch, "E832", {"start": v(-10.05, 16.4) * mm, "end": v(-10.27, 15.95) * mm});
            skLineSegment(sketch, "E833", {"start": v(-10.27, 15.95) * mm, "end": v(-10.4, 15.7) * mm});
            skLineSegment(sketch, "E834", {"start": v(-10.4, 15.7) * mm, "end": v(-10.49, 15.48) * mm});
            skLineSegment(sketch, "E835", {"start": v(-10.49, 15.48) * mm, "end": v(-10.54, 15.36) * mm});
            skLineSegment(sketch, "E836", {"start": v(-10.54, 15.36) * mm, "end": v(-10.55, 15.3) * mm});
            skLineSegment(sketch, "E837", {"start": v(-10.55, 15.3) * mm, "end": v(-10.55, 15.3) * mm});
            skLineSegment(sketch, "E838", {"start": v(-10.55, 15.3) * mm, "end": v(-10.53, 15.32) * mm});
            skLineSegment(sketch, "E839", {"start": v(-10.53, 15.32) * mm, "end": v(-10.2, 15.58) * mm});
            skLineSegment(sketch, "E840", {"start": v(-6.62, 15.62) * mm, "end": v(-6.34, 15.6) * mm});
            skLineSegment(sketch, "E841", {"start": v(-6.34, 15.6) * mm, "end": v(-6.23, 15.52) * mm});
            skLineSegment(sketch, "E842", {"start": v(-6.23, 15.52) * mm, "end": v(-6.14, 15.39) * mm});
            skLineSegment(sketch, "E843", {"start": v(-6.14, 15.39) * mm, "end": v(-6.02, 15.12) * mm});
            skLineSegment(sketch, "E844", {"start": v(-6.02, 15.12) * mm, "end": v(-5.92, 14.74) * mm});
            skLineSegment(sketch, "E845", {"start": v(-5.92, 14.74) * mm, "end": v(-5.81, 14.2) * mm});
            skLineSegment(sketch, "E846", {"start": v(-5.81, 14.2) * mm, "end": v(-5.71, 13.68) * mm});
            skLineSegment(sketch, "E847", {"start": v(-5.71, 13.68) * mm, "end": v(-5.63, 13.32) * mm});
            skLineSegment(sketch, "E848", {"start": v(-6.01, 16.46) * mm, "end": v(-6.08, 16.4) * mm});
            skLineSegment(sketch, "E849", {"start": v(-6.08, 16.4) * mm, "end": v(-6.2, 16.28) * mm});
            skLineSegment(sketch, "E850", {"start": v(-6.2, 16.28) * mm, "end": v(-6.36, 16.1) * mm});
            skLineSegment(sketch, "E851", {"start": v(-6.36, 16.1) * mm, "end": v(-6.54, 15.9) * mm});
            skLineSegment(sketch, "E852", {"start": v(-6.54, 15.9) * mm, "end": v(-6.73, 15.68) * mm});
            skLineSegment(sketch, "E853", {"start": v(-6.73, 15.68) * mm, "end": v(-6.78, 15.63) * mm});
            skLineSegment(sketch, "E854", {"start": v(-6.78, 15.63) * mm, "end": v(-6.79, 15.62) * mm});
            skLineSegment(sketch, "E855", {"start": v(-6.79, 15.62) * mm, "end": v(-6.79, 15.61) * mm});
            skLineSegment(sketch, "E856", {"start": v(-6.79, 15.61) * mm, "end": v(-6.79, 15.61) * mm});
            skLineSegment(sketch, "E857", {"start": v(-6.79, 15.61) * mm, "end": v(-6.8, 15.61) * mm});
            skLineSegment(sketch, "E858", {"start": v(-6.8, 15.61) * mm, "end": v(-6.79, 15.61) * mm});
            skLineSegment(sketch, "E859", {"start": v(-6.79, 15.61) * mm, "end": v(-6.78, 15.6) * mm});
            skLineSegment(sketch, "E860", {"start": v(-6.78, 15.6) * mm, "end": v(-6.62, 15.62) * mm});
            skLineSegment(sketch, "E861", {"start": v(-5.52, 6.7) * mm, "end": v(-5.4, 6.5) * mm});
            skLineSegment(sketch, "E862", {"start": v(-5.4, 6.5) * mm, "end": v(-5.27, 6.33) * mm});
            skLineSegment(sketch, "E863", {"start": v(-5.27, 6.33) * mm, "end": v(-5.17, 6.23) * mm});
            skLineSegment(sketch, "E864", {"start": v(-5.17, 6.23) * mm, "end": v(-5.14, 6.2) * mm});
            skLineSegment(sketch, "E865", {"start": v(-5.14, 6.2) * mm, "end": v(-5.12, 6.2) * mm});
            skLineSegment(sketch, "E866", {"start": v(-5.12, 6.2) * mm, "end": v(-5.09, 6.23) * mm});
            skLineSegment(sketch, "E867", {"start": v(-5.09, 6.23) * mm, "end": v(-5.05, 6.31) * mm});
            skLineSegment(sketch, "E868", {"start": v(-5.05, 6.31) * mm, "end": v(-4.98, 6.68) * mm});
            skLineSegment(sketch, "E869", {"start": v(-4.98, 6.68) * mm, "end": v(-4.95, 6.96) * mm});
            skLineSegment(sketch, "E870", {"start": v(-4.95, 6.96) * mm, "end": v(-4.95, 7.03) * mm});
            skLineSegment(sketch, "E871", {"start": v(-4.95, 7.03) * mm, "end": v(-4.96, 7.06) * mm});
            skLineSegment(sketch, "E872", {"start": v(-4.96, 7.06) * mm, "end": v(-4.97, 7.07) * mm});
            skLineSegment(sketch, "E873", {"start": v(-4.97, 7.07) * mm, "end": v(-4.98, 7.07) * mm});
            skLineSegment(sketch, "E874", {"start": v(-4.98, 7.07) * mm, "end": v(-5, 7.03) * mm});
            skLineSegment(sketch, "E875", {"start": v(-5, 7.03) * mm, "end": v(-5.03, 6.98) * mm});
            skLineSegment(sketch, "E876", {"start": v(-5.03, 6.98) * mm, "end": v(-5.16, 6.76) * mm});
            skLineSegment(sketch, "E877", {"start": v(-5.16, 6.76) * mm, "end": v(-5.26, 6.7) * mm});
            skLineSegment(sketch, "E878", {"start": v(-5.26, 6.7) * mm, "end": v(-5.28, 6.7) * mm});
            skLineSegment(sketch, "E879", {"start": v(-5.28, 6.7) * mm, "end": v(-5.3, 6.72) * mm});
            skLineSegment(sketch, "E880", {"start": v(-5.3, 6.72) * mm, "end": v(-5.36, 6.76) * mm});
            skLineSegment(sketch, "E881", {"start": v(-5.36, 6.76) * mm, "end": v(-5.47, 6.86) * mm});
            skLineSegment(sketch, "E882", {"start": v(-5.47, 6.86) * mm, "end": v(-5.58, 6.96) * mm});
            skLineSegment(sketch, "E883", {"start": v(-5.58, 6.96) * mm, "end": v(-5.6, 6.98) * mm});
            skLineSegment(sketch, "E884", {"start": v(-5.6, 6.98) * mm, "end": v(-5.62, 6.98) * mm});
            skLineSegment(sketch, "E885", {"start": v(-5.62, 6.98) * mm, "end": v(-5.63, 6.97) * mm});
            skLineSegment(sketch, "E886", {"start": v(-5.63, 6.97) * mm, "end": v(-5.63, 6.95) * mm});
            skLineSegment(sketch, "E887", {"start": v(-5.63, 6.95) * mm, "end": v(-5.6, 6.84) * mm});
            skLineSegment(sketch, "E888", {"start": v(-5.6, 6.84) * mm, "end": v(-5.52, 6.7) * mm});
            skLineSegment(sketch, "E889", {"start": v(-1.5, 10.1) * mm, "end": v(-1.1, 10.27) * mm});
            skLineSegment(sketch, "E890", {"start": v(-1.1, 10.27) * mm, "end": v(-0.66, 10.48) * mm});
            skLineSegment(sketch, "E891", {"start": v(-0.66, 10.48) * mm, "end": v(-0.34, 10.56) * mm});
            skLineSegment(sketch, "E892", {"start": v(-0.34, 10.56) * mm, "end": v(-0.14, 10.56) * mm});
            skLineSegment(sketch, "E893", {"start": v(-0.14, 10.56) * mm, "end": v(0.07, 10.48) * mm});
            skLineSegment(sketch, "E894", {"start": v(0.07, 10.48) * mm, "end": v(0.26, 10.35) * mm});
            skLineSegment(sketch, "E895", {"start": v(0.26, 10.35) * mm, "end": v(0.5, 10.16) * mm});
            skLineSegment(sketch, "E896", {"start": v(0.5, 10.16) * mm, "end": v(1.2, 9.45) * mm});
            skLineSegment(sketch, "E897", {"start": v(1.2, 9.45) * mm, "end": v(1.8, 8.58) * mm});
            skLineSegment(sketch, "E898", {"start": v(1.8, 8.58) * mm, "end": v(2.3, 7.54) * mm});
            skLineSegment(sketch, "E899", {"start": v(2.3, 7.54) * mm, "end": v(2.63, 6.6) * mm});
            skLineSegment(sketch, "E900", {"start": v(2.63, 6.6) * mm, "end": v(2.9, 5.54) * mm});
            skLineSegment(sketch, "E901", {"start": v(2.9, 5.54) * mm, "end": v(3.1, 4.38) * mm});
            skLineSegment(sketch, "E902", {"start": v(3.1, 4.38) * mm, "end": v(3.16, 4.08) * mm});
            skLineSegment(sketch, "E903", {"start": v(3.16, 4.08) * mm, "end": v(3.19, 3.96) * mm});
            skLineSegment(sketch, "E904", {"start": v(3.19, 3.96) * mm, "end": v(3.2, 3.96) * mm});
            skLineSegment(sketch, "E905", {"start": v(3.2, 3.96) * mm, "end": v(3.2, 3.95) * mm});
            skLineSegment(sketch, "E906", {"start": v(3.2, 3.95) * mm, "end": v(3.2, 3.96) * mm});
            skLineSegment(sketch, "E907", {"start": v(3.2, 3.96) * mm, "end": v(3.2, 3.97) * mm});
            skLineSegment(sketch, "E908", {"start": v(3.2, 3.97) * mm, "end": v(3.23, 4.02) * mm});
            skLineSegment(sketch, "E909", {"start": v(3.23, 4.02) * mm, "end": v(3.28, 4.2) * mm});
            skLineSegment(sketch, "E910", {"start": v(3.28, 4.2) * mm, "end": v(3.34, 4.46) * mm});
            skLineSegment(sketch, "E911", {"start": v(3.34, 4.46) * mm, "end": v(3.4, 4.78) * mm});
            skLineSegment(sketch, "E912", {"start": v(3.4, 4.78) * mm, "end": v(3.5, 5.26) * mm});
            skLineSegment(sketch, "E913", {"start": v(3.5, 5.26) * mm, "end": v(3.58, 5.74) * mm});
            skLineSegment(sketch, "E914", {"start": v(3.58, 5.74) * mm, "end": v(3.63, 6.16) * mm});
            skLineSegment(sketch, "E915", {"start": v(3.63, 6.16) * mm, "end": v(3.65, 6.49) * mm});
            skLineSegment(sketch, "E916", {"start": v(3.65, 6.49) * mm, "end": v(3.66, 6.89) * mm});
            skLineSegment(sketch, "E917", {"start": v(3.66, 6.89) * mm, "end": v(3.65, 7.3) * mm});
            skLineSegment(sketch, "E918", {"start": v(3.65, 7.3) * mm, "end": v(3.62, 7.73) * mm});
            skLineSegment(sketch, "E919", {"start": v(3.62, 7.73) * mm, "end": v(3.58, 8.02) * mm});
            skLineSegment(sketch, "E920", {"start": v(3.58, 8.02) * mm, "end": v(3.49, 8.33) * mm});
            skLineSegment(sketch, "E921", {"start": v(3.49, 8.33) * mm, "end": v(3.35, 8.69) * mm});
            skLineSegment(sketch, "E922", {"start": v(3.35, 8.69) * mm, "end": v(3.1, 9.25) * mm});
            skArc(sketch, "E923", {"start": v(2.94, 9.58) * mm, "mid": v(3.02, 9.41) * mm, "end": v(3.1, 9.25) * mm});
            skLineSegment(sketch, "E924", {"start": v(2.94, 9.58) * mm, "end": v(2.94, 9.58) * mm});
            skLineSegment(sketch, "E925", {"start": v(2.94, 9.58) * mm, "end": v(2.96, 9.58) * mm});
            skLineSegment(sketch, "E926", {"start": v(2.96, 9.58) * mm, "end": v(3.13, 9.44) * mm});
            skLineSegment(sketch, "E927", {"start": v(3.13, 9.44) * mm, "end": v(3.28, 9.3) * mm});
            skLineSegment(sketch, "E928", {"start": v(3.28, 9.3) * mm, "end": v(3.33, 9.28) * mm});
            skLineSegment(sketch, "E929", {"start": v(3.33, 9.28) * mm, "end": v(3.34, 9.27) * mm});
            skLineSegment(sketch, "E930", {"start": v(3.34, 9.27) * mm, "end": v(3.35, 9.27) * mm});
            skLineSegment(sketch, "E931", {"start": v(3.35, 9.27) * mm, "end": v(3.36, 9.27) * mm});
            skLineSegment(sketch, "E932", {"start": v(3.36, 9.27) * mm, "end": v(3.36, 9.28) * mm});
            skLineSegment(sketch, "E933", {"start": v(3.36, 9.28) * mm, "end": v(3.37, 9.31) * mm});
            skLineSegment(sketch, "E934", {"start": v(3.37, 9.31) * mm, "end": v(3.36, 9.41) * mm});
            skLineSegment(sketch, "E935", {"start": v(3.36, 9.41) * mm, "end": v(3.33, 9.57) * mm});
            skLineSegment(sketch, "E936", {"start": v(3.33, 9.57) * mm, "end": v(3.25, 9.94) * mm});
            skLineSegment(sketch, "E937", {"start": v(3.25, 9.94) * mm, "end": v(2.93, 10.91) * mm});
            skLineSegment(sketch, "E938", {"start": v(2.93, 10.91) * mm, "end": v(2.53, 11.76) * mm});
            skLineSegment(sketch, "E939", {"start": v(2.53, 11.76) * mm, "end": v(2.9, 11.3) * mm});
            skLineSegment(sketch, "E940", {"start": v(2.9, 11.3) * mm, "end": v(3.12, 10.97) * mm});
            skLineSegment(sketch, "E941", {"start": v(3.2, 10.98) * mm, "end": v(3.18, 11.26) * mm});
            skLineSegment(sketch, "E942", {"start": v(3.18, 11.26) * mm, "end": v(3.12, 11.85) * mm});
            skLineSegment(sketch, "E943", {"start": v(3.12, 11.85) * mm, "end": v(3, 12.4) * mm});
            skLineSegment(sketch, "E944", {"start": v(3, 12.4) * mm, "end": v(2.68, 13.26) * mm});
            skLineSegment(sketch, "E945", {"start": v(2.68, 13.26) * mm, "end": v(2.6, 13.43) * mm});
            skLineSegment(sketch, "E946", {"start": v(2.6, 13.43) * mm, "end": v(2.53, 13.55) * mm});
            skLineSegment(sketch, "E947", {"start": v(2.53, 13.55) * mm, "end": v(2.35, 13.88) * mm});
            skLineSegment(sketch, "E948", {"start": v(2.62, 13.91) * mm, "end": v(2.35, 13.88) * mm});
            skLineSegment(sketch, "E949", {"start": v(3.2, 10.98) * mm, "end": v(3.19, 10.95) * mm});
            skLineSegment(sketch, "E950", {"start": v(3.19, 10.95) * mm, "end": v(3.17, 10.94) * mm});
            skLineSegment(sketch, "E951", {"start": v(3.17, 10.94) * mm, "end": v(3.15, 10.95) * mm});
            skLineSegment(sketch, "E952", {"start": v(3.15, 10.95) * mm, "end": v(3.12, 10.97) * mm});
            skLineSegment(sketch, "E953", {"start": v(-6.03, 16.9) * mm, "end": v(-5.68, 16.8) * mm});
            skLineSegment(sketch, "E954", {"start": v(-5.68, 16.8) * mm, "end": v(-5.88, 16.6) * mm});
            skLineSegment(sketch, "E955", {"start": v(-5.88, 16.6) * mm, "end": v(-6.01, 16.46) * mm});
            skSolve(sketch);
        }
        {
            var Q0;
            Q0=makeQuery(id+"F6.imprint","IMPRINT",FACE,{"disambiguationData":[TD([[makeQuery(id+"F6.imprint","IMPRINT",EDGE,{"derivedFrom":sQuery(id+"F6.wireOp",EDGE,"E397")}),1.0]])]});
            extrude(context, id + "F7", {"entities" : qUnion([Q0]), "operationType" : NewBodyOperationType.REMOVE, "oppositeDirection" : true, "depth" : 0.75 * mm, "offsetDistance" : 25 * mm});
        }
        {
            var Q0;
            Q0=makeQuery(id+"F5.opExtrude","SWEPT_FACE",FACE,{"disambiguationData":[OSD([sQuery(id+"F4.wireOp",EDGE,"E0")])]});
            var sketch = newSketch(context, id + "F8", { "sketchPlane" : qUnion([Q0])});
            skLineSegment(sketch, "E956.bottom", {"start": v(4.12, 7.5) * mm, "end": v(10.12, 7.5) * mm});
            skLineSegment(sketch, "E956.top", {"start": v(4.12, 22.5) * mm, "end": v(10.12, 22.5) * mm});
            skLineSegment(sketch, "E956.left", {"start": v(4.12, 7.5) * mm, "end": v(4.12, 22.5) * mm});
            skLineSegment(sketch, "E956.right", {"start": v(10.12, 7.5) * mm, "end": v(10.12, 22.5) * mm});
            skPoint(sketch, "E957", {"position": v(4.12, 15) * mm});
            skPoint(sketch, "E958", {"position": v(10.12, 15) * mm});
            skLineSegment(sketch, "E959", {"start": v(13.1, 15) * mm, "end": v(2.03, 15) * mm, "construction": true});
            skSolve(sketch);
        }
        {
            var Q0;
            Q0=makeQuery(id+"F8.imprint","IMPRINT",FACE,{"disambiguationData":[TD([[makeQuery(id+"F8.imprint","IMPRINT",EDGE,{"derivedFrom":sQuery(id+"F8.wireOp",EDGE,"E956.bottom")}),1.0]])]});
            var Q1;
            Q1 = qConstructionFilter(qBodyType(qCreatedBy(id + "F8" ,EDGE), BodyType.WIRE), ConstructionObject.NO);
            extrude(context, id + "F9", {"entities" : qUnion([Q0]), "operationType" : NewBodyOperationType.REMOVE, "surfaceEntities" : qUnion([Q1]), "oppositeDirection" : true, "depth" : getVariable(context, 'SmallThickness'), "offsetDistance" : 25 * mm});
        }
        {
            var Q0;
            Q0=makeQuery(id+"F5.opExtrude","SWEPT_EDGE",EDGE,{"disambiguationData":[OSD([sQuery(id+"F4.wireOp",EDGE,"E6"),sQuery(id+"F4.wireOp",EDGE,"E7")])]});
            var Q1;
            Q1=makeQuery(id+"F5.opExtrude","SWEPT_EDGE",EDGE,{"disambiguationData":[OSD([sQuery(id+"F4.wireOp",EDGE,"KsOauwYz-KTQx-rG80-Thxc-iWJnzNues2s5"),sQuery(id+"F4.wireOp",EDGE,"E0")])]});
            var Q2;
            Q2=makeQuery(id+"F5.opExtrude","SWEPT_EDGE",EDGE,{"disambiguationData":[OSD([sQuery(id+"F4.wireOp",EDGE,"E6"),sQuery(id+"F4.wireOp",EDGE,"E11")])]});
            var Q3;
            Q3=makeQuery(id+"F5.opExtrude","SWEPT_EDGE",EDGE,{"disambiguationData":[OSD([sQuery(id+"F4.wireOp",EDGE,"E0"),sQuery(id+"F4.wireOp",EDGE,"E15")])]});
            var Q4;
            Q4=makeQuery(id+"F5.opExtrude","SWEPT_EDGE",EDGE,{"disambiguationData":[OSD([sQuery(id+"F4.wireOp",EDGE,"E20"),sQuery(id+"F4.wireOp",EDGE,"E21")])]});
            fillet(context, id + "F10", {"entities" : qUnion([Q0, Q1, Q2, Q3, Q4]), "radius" : (getVariable(context, 'OuterFilet')) * mm, "tangentPropagation" : true, "allowEdgeOverflow" : false});
        }
        {
            var Q0;
            Q0=makeQuery(id+"F5.opExtrude","SWEPT_EDGE",EDGE,{"disambiguationData":[OSD([sQuery(id+"F4.wireOp",EDGE,"E8"),sQuery(id+"F4.wireOp",EDGE,"E9")])]});
            var Q1;
            Q1=makeQuery(id+"F5.opExtrude","SWEPT_EDGE",EDGE,{"disambiguationData":[OSD([sQuery(id+"F4.wireOp",EDGE,"E9"),sQuery(id+"F4.wireOp",EDGE,"E17")])]});
            var Q2;
            Q2=makeQuery(id+"F5.opExtrude","SWEPT_EDGE",EDGE,{"disambiguationData":[OSD([sQuery(id+"F4.wireOp",EDGE,"E8"),sQuery(id+"F4.wireOp",EDGE,"E17")])]});
            var Q3;
            Q3=makeQuery(id+"F5.opExtrude","SWEPT_EDGE",EDGE,{"disambiguationData":[OSD([sQuery(id+"F4.wireOp",EDGE,"E13"),sQuery(id+"F4.wireOp",EDGE,"E14")])]});
            var Q4;
            Q4=makeQuery(id+"F5.opExtrude","SWEPT_EDGE",EDGE,{"disambiguationData":[OSD([sQuery(id+"F4.wireOp",EDGE,"E3"),sQuery(id+"F4.wireOp",EDGE,"E7")])]});
            var Q5;
            Q5=makeQuery(id+"F5.opExtrude","SWEPT_EDGE",EDGE,{"disambiguationData":[OSD([sQuery(id+"F4.wireOp",EDGE,"KsOauwYz-KTQx-rG80-Thxc-iWJnzNues2s5"),sQuery(id+"F4.wireOp",EDGE,"E3")])]});
            var Q6;
            Q6=makeQuery(id+"F5.opExtrude","SWEPT_EDGE",EDGE,{"disambiguationData":[OSD([sQuery(id+"F4.wireOp",EDGE,"E1"),sQuery(id+"F4.wireOp",EDGE,"E19")])]});
            var Q7;
            Q7=makeQuery(id+"F5.opExtrude","SWEPT_EDGE",EDGE,{"disambiguationData":[OSD([sQuery(id+"F4.wireOp",EDGE,"E1"),sQuery(id+"F4.wireOp",EDGE,"E16")])]});
            var Q8;
            Q8=makeQuery(id+"F5.opExtrude","SWEPT_EDGE",EDGE,{"disambiguationData":[OSD([sQuery(id+"F4.wireOp",EDGE,"E2"),sQuery(id+"F4.wireOp",EDGE,"E16")])]});
            var Q9;
            {var subQ0=sQuery(id+"F4.wireOp",EDGE,"E19");var subQ1=makeQuery(id+"F5.opExtrude","SWEPT_FACE",FACE,{"disambiguationData":[OSD([subQ0])]});var subQ2=sQuery(id+"F8.wireOp",EDGE,"E956.bottom");var subQ3=sQuery(id+"F4.wireOp",EDGE,"E2");var subQ4=makeQuery(id+"F5.opExtrude","SWEPT_FACE",FACE,{"disambiguationData":[OSD([subQ3])]});Q9=makeQuery(id+"F9.boolean.opBoolean","SPLIT",EDGE,{"disambiguationData":[topologyDisambiguationEdgeConnected([subQ4,subQ1]),TD([makeQuery(id+"F9.opExtrude","SWEPT_FACE",FACE,{"disambiguationData":[OSD([subQ2])]})])],"derivedFrom":makeQuery(id+"F5.opExtrude","SWEPT_EDGE",EDGE,{"disambiguationData":[OSD([subQ3,subQ0])]})});}
            var Q10;
            Q10=makeQuery(id+"F9.boolean.opBoolean","COPY",EDGE,{"derivedFrom":makeQuery(id+"F9.opExtrude","SWEPT_EDGE",EDGE,{"disambiguationData":[OSD([sQuery(id+"F8.wireOp",EDGE,"E956.bottom"),sQuery(id+"F8.wireOp",EDGE,"E956.left")])]})});
            var Q11;
            Q11=makeQuery(id+"F9.boolean.opBoolean","COPY",EDGE,{"derivedFrom":makeQuery(id+"F9.opExtrude","SWEPT_EDGE",EDGE,{"disambiguationData":[OSD([sQuery(id+"F8.wireOp",EDGE,"E956.bottom"),sQuery(id+"F8.wireOp",EDGE,"E956.right")])]})});
            var Q12;
            Q12=makeQuery(id+"F9.boolean.opBoolean","COPY",EDGE,{"derivedFrom":makeQuery(id+"F9.opExtrude","SWEPT_EDGE",EDGE,{"disambiguationData":[OSD([sQuery(id+"F8.wireOp",EDGE,"E956.top"),sQuery(id+"F8.wireOp",EDGE,"E956.right")])]})});
            var Q13;
            Q13=makeQuery(id+"F9.boolean.opBoolean","COPY",EDGE,{"derivedFrom":makeQuery(id+"F9.opExtrude","SWEPT_EDGE",EDGE,{"disambiguationData":[OSD([sQuery(id+"F8.wireOp",EDGE,"E956.top"),sQuery(id+"F8.wireOp",EDGE,"E956.left")])]})});
            fillet(context, id + "F11", {"entities" : qUnion([Q0, Q1, Q2, Q3, Q4, Q5, Q6, Q7, Q8, Q9, Q10, Q11, Q12, Q13]), "radius" : getVariable(context, 'InnerFilet'), "tangentPropagation" : true, "allowEdgeOverflow" : false});
        }
    });
